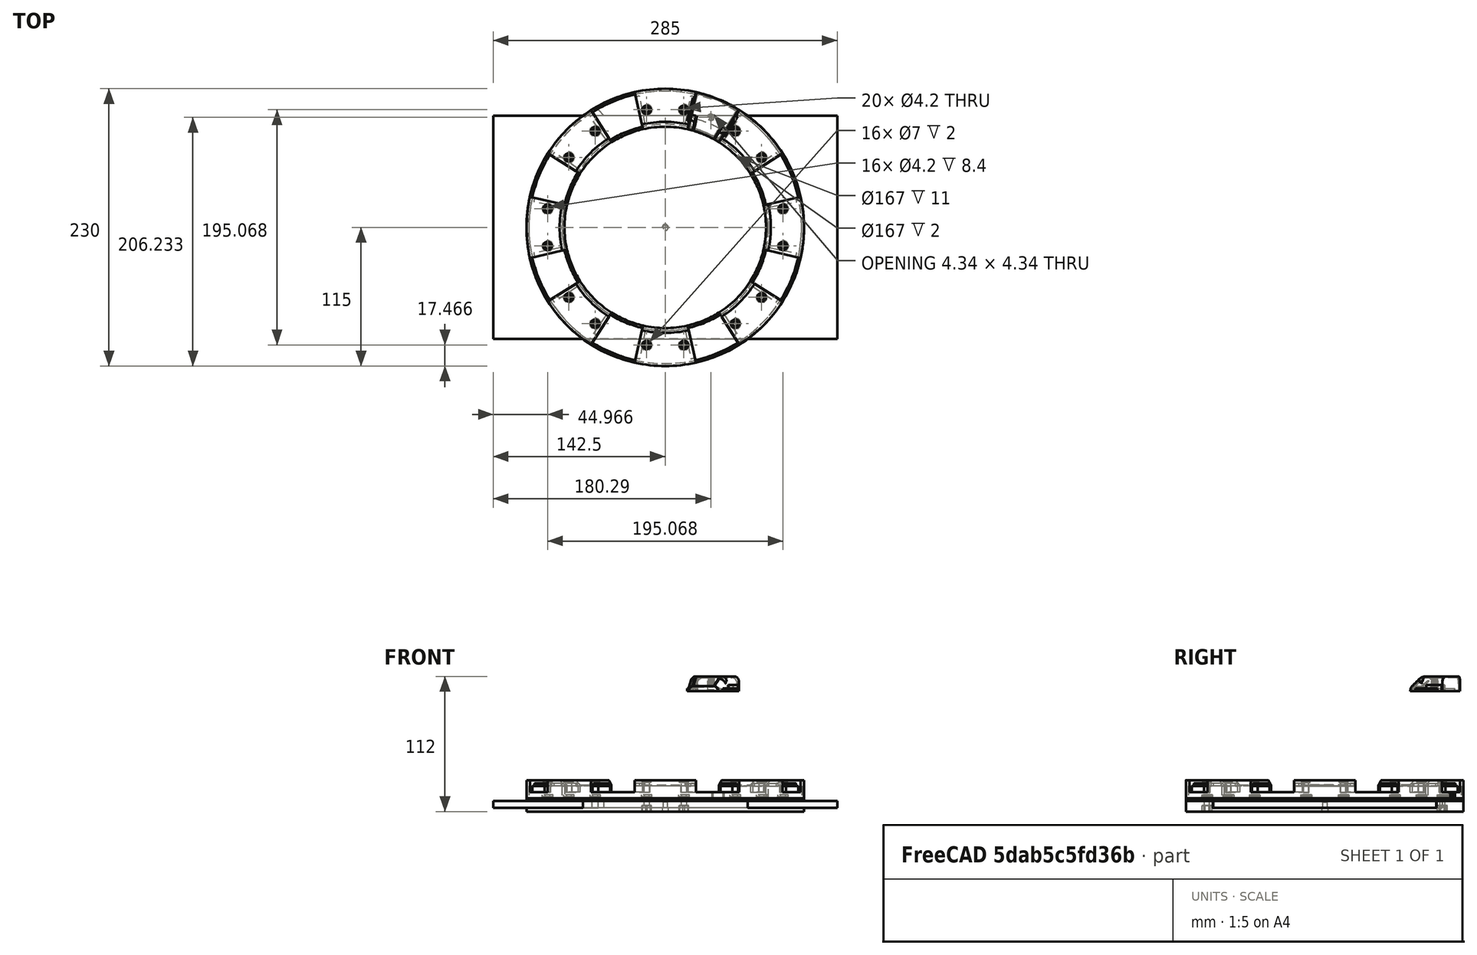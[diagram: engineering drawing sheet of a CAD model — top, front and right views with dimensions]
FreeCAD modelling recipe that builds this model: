
FCSTD DOCUMENT  (FreeCAD 1.0R39319 (Git))
Label: Mamai
License: All rights reserved
LicenseURL: https://en.wikipedia.org/wiki/All_rights_reserved
objects: Sketcher::SketchObject×45, PartDesign::Pad×23, PartDesign::Pocket×16, PartDesign::Body×8, PartDesign::Plane×7, PartDesign::Line×6, PartDesign::Fillet×6, PartDesign::Chamfer×4, PartDesign::Thickness×2, Image::ImagePlane×1, Mesh::Feature×1
note: 264 computed .brp shape members not serialized (recipe doc carries the construction recipe); baked Part::Feature solids carry a one-line shape summary decoded from their .brp

FEATURE [Image::ImagePlane] step4_tip2  label="step4-tip2"
  Placement = pos=(0,0,1000) rot=(0,0,1;0rad)
  XSize = 245
  YSize = 245
FEATURE [Mesh::Feature] pcb
  Placement = pos=(126,214.5,10) rot=(0,0,-1;1.1781rad)
FEATURE [Sketcher::SketchObject] Sketch
  ArcFitTolerance = 1e-06
  AttachmentSupport = -> [XY_Plane]
  FullyConstrained = false
  MakeInternals = false
  MapMode = 5
  sketch-geometry (10):
    g0: LineSegment StartX=0 StartY=-1e-16 StartZ=0 EndX=2e-16 EndY=-1e-16 EndZ=0
    g1: LineSegment StartX=0 StartY=-1e-16 StartZ=0 EndX=0 EndY=0 EndZ=0
    g2: LineSegment StartX=0 StartY=0 StartZ=0 EndX=2e-16 EndY=0 EndZ=0
    g3: LineSegment StartX=0 StartY=0 StartZ=0 EndX=0 EndY=-1e-16 EndZ=0
    g4: GeomPoint [constr] X=0 Y=0 Z=0
    g5: LineSegment StartX=-92.5 StartY=-142.5 StartZ=0 EndX=92.5 EndY=-142.5 EndZ=0
    g6: LineSegment StartX=92.5 StartY=-142.5 StartZ=0 EndX=92.5 EndY=142.5 EndZ=0
    g7: LineSegment StartX=92.5 StartY=142.5 StartZ=0 EndX=-92.5 EndY=142.5 EndZ=0
    g8: LineSegment StartX=-92.5 StartY=142.5 StartZ=0 EndX=-92.5 EndY=-142.5 EndZ=0
    g9: GeomPoint [constr] X=0 Y=0 Z=0
  constraints (21):
    c: Coincident(g0,g1)
    c: Coincident(g1,g2)
    c: Coincident(g2,g3)
    c: Coincident(g3,g0)
    c: Horizontal(g0)
    c: Horizontal(g2)
    c: Vertical(g1)
    c: Vertical(g3)
    c: Symmetric(g2,g0,g4)
    c: Coincident(g5,g6)
    c: Coincident(g6,g7)
    c: Coincident(g7,g8)
    c: Coincident(g8,g5)
    c: Horizontal(g5)
    c: Horizontal(g7)
    c: Vertical(g6)
    c: Vertical(g8)
    c: Symmetric(g7,g5,g9)
    c: Distance(g6,g8) = 185
    c: Distance(g5,g7) = 285
    c: Coincident(g9,g4)
FEATURE [PartDesign::Body] Body  label="Other"
  AllowCompound = false
  Group = -> [Sketch]
  Origin = -> Origin
FEATURE [Sketcher::SketchObject] Sketch001
  ArcFitTolerance = 1e-06
  AttachmentSupport = -> [XY_Plane001]
  FullyConstrained = true
  MakeInternals = false
  MapMode = 5
  sketch-geometry (5):
    g0: LineSegment StartX=-142.5 StartY=-92.5 StartZ=0 EndX=142.5 EndY=-92.5 EndZ=0
    g1: LineSegment StartX=142.5 StartY=-92.5 StartZ=0 EndX=142.5 EndY=92.5 EndZ=0
    g2: LineSegment StartX=142.5 StartY=92.5 StartZ=0 EndX=-142.5 EndY=92.5 EndZ=0
    g3: LineSegment StartX=-142.5 StartY=92.5 StartZ=0 EndX=-142.5 EndY=-92.5 EndZ=0
    g4: GeomPoint [constr] X=0 Y=0 Z=0
  constraints (12):
    c: Coincident(g0,g1)
    c: Coincident(g1,g2)
    c: Coincident(g2,g3)
    c: Coincident(g3,g0)
    c: Horizontal(g0)
    c: Horizontal(g2)
    c: Vertical(g1)
    c: Vertical(g3)
    c: Symmetric(g2,g0,g4)
    c: Distance(g1,g3) = 285
    c: Distance(g0,g2) = 185
    c: Coincident(g4,g-1)
FEATURE [PartDesign::Pad] Pad
  Direction = (0,0,1)
  Length = 5.7
  Length2 = 10
  Profile = -> Sketch001
  ReferenceAxis = -> Sketch001 [N_Axis]
  Refine = true
  Suppressed = false
  Type = 0
FEATURE [PartDesign::Body] Body001  label="Tablet"
  AllowCompound = false
  Group = -> [Sketch001,Pad]
  Origin = -> Origin001
  Placement = pos=(0,0,3) rot=(0,0,1;0rad)
  Tip = -> Pad
FEATURE [Sketcher::SketchObject] Sketch002
  ArcFitTolerance = 1e-06
  AttachmentSupport = -> [XY_Plane002]
  FullyConstrained = false
  MakeInternals = false
  MapMode = 5
  sketch-geometry (11):
    g0: LineSegment [constr] StartX=-142.5 StartY=-92.5 StartZ=0 EndX=142.5 EndY=-92.5 EndZ=0
    g1: LineSegment [constr] StartX=142.5 StartY=-92.5 StartZ=0 EndX=142.5 EndY=92.5 EndZ=0
    g2: LineSegment [constr] StartX=142.5 StartY=92.5 StartZ=0 EndX=68.3283 EndY=92.5 EndZ=0
    g3: LineSegment [constr] StartX=-142.5 StartY=92.5 StartZ=0 EndX=-142.5 EndY=-92.5 EndZ=0
    g4: GeomPoint [constr] X=0 Y=0 Z=0
    g5: LineSegment [constr] StartX=-133.5 StartY=83.5 StartZ=0 EndX=-133.5 EndY=-83.5 EndZ=0
    g6: LineSegment [constr] StartX=-133.5 StartY=-83.5 StartZ=0 EndX=133.5 EndY=-83.5 EndZ=0
    g7: LineSegment [constr] StartX=133.5 StartY=-83.5 StartZ=0 EndX=133.5 EndY=83.5 EndZ=0
    g8: LineSegment [constr] StartX=133.5 StartY=83.5 StartZ=0 EndX=-133.5 EndY=83.5 EndZ=0
    g9: LineSegment [constr] StartX=68.3283 StartY=92.5 StartZ=0 EndX=-142.5 EndY=92.5 EndZ=0
    g10: Circle CenterX=0 CenterY=0 CenterZ=0 NormalX=0 NormalY=0 NormalZ=1 AngleXU=0 Radius=115
  constraints (28):
    c: Coincident(g0,g1)
    c: Coincident(g1,g2)
    c: Coincident(g3,g0)
    c: Horizontal(g0)
    c: Horizontal(g2)
    c: Vertical(g1)
    c: Vertical(g3)
    c: Symmetric(g2,g0,g4)
    c: Distance(g1,g3) = 285
    c: Distance(g0,g3) = 185
    c: Coincident(g4,g-1)
    c: Coincident(g5,g6)
    c: Coincident(g6,g7)
    c: Coincident(g7,g8)
    c: Coincident(g8,g5)
    c: Vertical(g5)
    c: Vertical(g7)
    c: Horizontal(g6)
    c: Horizontal(g8)
    c: Distance(g3,g5) = 9
    c: Distance(g8,g2) = 9
    c: Distance(g0,g6) = 9
    c: Distance(g1,g7) = 9
    c: Coincident(g9,g2)
    c: Coincident(g9,g3)
    c: Horizontal(g9)
    c: Coincident(g10,g4)
    c: Diameter(g10) = 230
FEATURE [PartDesign::Pad] Pad001
  Direction = (0,0,1)
  Length = 8.7
  Length2 = 10
  Profile = -> Sketch002
  ReferenceAxis = -> Sketch002 [N_Axis]
  Refine = true
  Suppressed = false
  Type = 0
FEATURE [PartDesign::Plane] DatumPlane
  AttachmentOffset = pos=(115,0,0) rot=(0,1,0;1.5708rad)
  AttachmentSupport = -> [Pad001]
  Length = 71.4441
  MapMode = 45
  Placement = pos=(115,-6e-15,4.35) rot=(0,1,0;1.5708rad)
  ResizeMode = 0
  Width = 251.368
FEATURE [Sketcher::SketchObject] Sketch005
  ArcFitTolerance = 1e-06
  AttachmentSupport = -> [DatumPlane]
  FullyConstrained = true
  MakeInternals = false
  MapMode = 5
  Placement = pos=(115,-6e-15,4.35) rot=(0,1,0;1.5708rad)
  sketch-geometry (5):
    g0: LineSegment StartX=-4.35 StartY=-92.6 StartZ=0 EndX=1.35 EndY=-92.6 EndZ=0
    g1: LineSegment StartX=1.35 StartY=-92.6 StartZ=0 EndX=1.35 EndY=92.6 EndZ=0
    g2: LineSegment StartX=1.35 StartY=92.6 StartZ=0 EndX=-4.35 EndY=92.6 EndZ=0
    g3: LineSegment StartX=-4.35 StartY=92.6 StartZ=0 EndX=-4.35 EndY=-92.6 EndZ=0
    g4: GeomPoint [constr] X=-1.5 Y=0 Z=0
  constraints (13):
    c: Coincident(g0,g1)
    c: Coincident(g1,g2)
    c: Coincident(g2,g3)
    c: Coincident(g3,g0)
    c: Horizontal(g0)
    c: Horizontal(g2)
    c: Vertical(g1)
    c: Vertical(g3)
    c: Symmetric(g2,g0,g4)
    c: Distance(g1,g3) = 5.7
    c: Distance(g0,g2) = 185.2
    c: PointOnObject(g4,g-1)
    c: DistanceX(g4,g-1) = 1.5
FEATURE [PartDesign::Pocket] Pocket
  BaseFeature = -> Pad001
  Direction = (-1,0,-2e-16)
  Length = 257
  Length2 = 5
  Profile = -> Sketch005
  ReferenceAxis = -> Sketch005 [N_Axis]
  Refine = true
  Suppressed = false
  Type = 0
FEATURE [Sketcher::SketchObject] Sketch006
  ArcFitTolerance = 1e-06
  AttachmentSupport = -> [XY_Plane003]
  FullyConstrained = true
  MakeInternals = false
  MapMode = 5
  sketch-geometry (1):
    g0: Circle CenterX=0 CenterY=0 CenterZ=0 NormalX=0 NormalY=0 NormalZ=1 AngleXU=0 Radius=115
  constraints (2):
    c: Diameter(g0) = 230
    c: Coincident(g0,g-1)
FEATURE [PartDesign::Pad] Pad002
  Direction = (0,0,1)
  Length = 2
  Length2 = 10
  Profile = -> Sketch006
  ReferenceAxis = -> Sketch006 [N_Axis]
  Refine = true
  Suppressed = false
  Type = 0
FEATURE [Sketcher::SketchObject] Sketch007
  ArcFitTolerance = 1e-06
  AttachmentSupport = -> [Pad002]
  FullyConstrained = true
  MakeInternals = false
  MapMode = 5
  Placement = pos=(0,0,2) rot=(0,0,1;0rad)
  sketch-geometry (6):
    g0: Circle CenterX=0 CenterY=0 CenterZ=0 NormalX=0 NormalY=0 NormalZ=1 AngleXU=0 Radius=83.5
    g1: LineSegment [constr] StartX=-142.5 StartY=-92.5 StartZ=0 EndX=142.5 EndY=-92.5 EndZ=0
    g2: LineSegment [constr] StartX=142.5 StartY=-92.5 StartZ=0 EndX=142.5 EndY=92.5 EndZ=0
    g3: LineSegment [constr] StartX=142.5 StartY=92.5 StartZ=0 EndX=-142.5 EndY=92.5 EndZ=0
    g4: LineSegment [constr] StartX=-142.5 StartY=92.5 StartZ=0 EndX=-142.5 EndY=-92.5 EndZ=0
    g5: GeomPoint [constr] X=0 Y=0 Z=0
  constraints (14):
    c: Coincident(g0,g-1)
    c: Coincident(g1,g2)
    c: Coincident(g2,g3)
    c: Coincident(g3,g4)
    c: Coincident(g4,g1)
    c: Horizontal(g1)
    c: Horizontal(g3)
    c: Vertical(g2)
    c: Vertical(g4)
    c: Symmetric(g3,g1,g5)
    c: Distance(g2,g4) = 285
    c: Distance(g1,g3) = 185
    c: Coincident(g5,g0)
    c: Distance(g0,g3) = 9
FEATURE [PartDesign::Pocket] Pocket001
  BaseFeature = -> Pad002
  Direction = (0,0,-1)
  Length = 5
  Length2 = 5
  Profile = -> Sketch007
  ReferenceAxis = -> Sketch007 [N_Axis]
  Refine = true
  Suppressed = false
  Type = 0
FEATURE [Sketcher::SketchObject] Sketch008
  ArcFitTolerance = 1e-06
  AttachmentSupport = -> [Pocket001]
  FullyConstrained = false
  MakeInternals = false
  MapMode = 5
  Placement = pos=(0,0,2) rot=(0,0,1;0rad)
  sketch-geometry (36):
    g0: LineSegment [constr] StartX=1.9e-05 StartY=-1.44227e-05 StartZ=0 EndX=97.5342 EndY=15.4479 EndZ=0
    g1: LineSegment [constr] StartX=-1.49389e-08 StartY=-2.44401e-07 StartZ=0 EndX=79.8904 EndY=58.0438 EndZ=0
    g2: LineSegment [constr] StartX=1.9e-05 StartY=-1.44227e-05 StartZ=0 EndX=58.0438 EndY=79.8904 EndZ=0
    g3: LineSegment [constr] StartX=-1.49389e-08 StartY=-2.44401e-07 StartZ=0 EndX=15.4479 EndY=97.5342 EndZ=0
    g4: ArcOfCircle [constr] CenterX=1.9e-05 CenterY=-1.44227e-05 CenterZ=0 NormalX=0 NormalY=0 NormalZ=1 AngleXU=0 Radius=98.75 StartAngle=4.28074e-09 EndAngle=1.5708
    g5: Circle CenterX=15.4479 CenterY=97.5342 CenterZ=0 NormalX=0 NormalY=0 NormalZ=1 AngleXU=0 Radius=2.1
    g6: Circle CenterX=58.0438 CenterY=79.8904 CenterZ=0 NormalX=0 NormalY=0 NormalZ=1 AngleXU=0 Radius=2.1
    g7: Circle CenterX=79.8904 CenterY=58.0438 CenterZ=0 NormalX=0 NormalY=0 NormalZ=1 AngleXU=0 Radius=2.1
    g8: Circle CenterX=97.5342 CenterY=15.4479 CenterZ=0 NormalX=0 NormalY=0 NormalZ=1 AngleXU=0 Radius=2.1
    g9: LineSegment [constr] StartX=1.9e-05 StartY=1.44227e-05 StartZ=0 EndX=97.5342 EndY=-15.4479 EndZ=0
    g10: LineSegment [constr] StartX=-1.49389e-08 StartY=2.44401e-07 StartZ=0 EndX=79.8904 EndY=-58.0438 EndZ=0
    g11: LineSegment [constr] StartX=1.9e-05 StartY=1.44227e-05 StartZ=0 EndX=58.0438 EndY=-79.8904 EndZ=0
    g12: LineSegment [constr] StartX=-1.49389e-08 StartY=2.44401e-07 StartZ=0 EndX=15.4479 EndY=-97.5342 EndZ=0
    g13: ArcOfCircle [constr] CenterX=1.9e-05 CenterY=1.44227e-05 CenterZ=0 NormalX=0 NormalY=0 NormalZ=1 AngleXU=0 Radius=98.75 StartAngle=4.71239 EndAngle=6.28319
    g14: Circle CenterX=15.4479 CenterY=-97.5342 CenterZ=0 NormalX=0 NormalY=0 NormalZ=1 AngleXU=0 Radius=2.1
    g15: Circle CenterX=58.0438 CenterY=-79.8904 CenterZ=0 NormalX=0 NormalY=0 NormalZ=1 AngleXU=0 Radius=2.1
    g16: Circle CenterX=79.8904 CenterY=-58.0438 CenterZ=0 NormalX=0 NormalY=0 NormalZ=1 AngleXU=0 Radius=2.1
    g17: Circle CenterX=97.5342 CenterY=-15.4479 CenterZ=0 NormalX=0 NormalY=0 NormalZ=1 AngleXU=0 Radius=2.1
    g18: LineSegment [constr] StartX=-1.9e-05 StartY=-1.44227e-05 StartZ=0 EndX=-97.5342 EndY=15.4479 EndZ=0
    g19: LineSegment [constr] StartX=1.49389e-08 StartY=-2.44401e-07 StartZ=0 EndX=-79.8904 EndY=58.0438 EndZ=0
    g20: LineSegment [constr] StartX=-1.9e-05 StartY=-1.44227e-05 StartZ=0 EndX=-58.0438 EndY=79.8904 EndZ=0
    g21: LineSegment [constr] StartX=1.49389e-08 StartY=-2.44401e-07 StartZ=0 EndX=-15.4479 EndY=97.5342 EndZ=0
    g22: ArcOfCircle [constr] CenterX=-1.9e-05 CenterY=-1.44227e-05 CenterZ=0 NormalX=0 NormalY=0 NormalZ=1 AngleXU=0 Radius=98.75 StartAngle=1.5708 EndAngle=3.14159
    g23: Circle CenterX=-15.4479 CenterY=97.5342 CenterZ=0 NormalX=0 NormalY=0 NormalZ=1 AngleXU=0 Radius=2.1
    g24: Circle CenterX=-58.0438 CenterY=79.8904 CenterZ=0 NormalX=0 NormalY=0 NormalZ=1 AngleXU=0 Radius=2.1
    g25: Circle CenterX=-79.8904 CenterY=58.0438 CenterZ=0 NormalX=0 NormalY=0 NormalZ=1 AngleXU=0 Radius=2.1
    g26: Circle CenterX=-97.5342 CenterY=15.4479 CenterZ=0 NormalX=0 NormalY=0 NormalZ=1 AngleXU=0 Radius=2.1
    g27: LineSegment [constr] StartX=-1.9e-05 StartY=1.44227e-05 StartZ=0 EndX=-97.5342 EndY=-15.4479 EndZ=0
    g28: LineSegment [constr] StartX=1.49389e-08 StartY=2.44401e-07 StartZ=0 EndX=-79.8904 EndY=-58.0438 EndZ=0
    g29: LineSegment [constr] StartX=-1.9e-05 StartY=1.44227e-05 StartZ=0 EndX=-58.0438 EndY=-79.8904 EndZ=0
    g30: LineSegment [constr] StartX=1.49389e-08 StartY=2.44401e-07 StartZ=0 EndX=-15.4479 EndY=-97.5342 EndZ=0
    g31: ArcOfCircle [constr] CenterX=-1.9e-05 CenterY=1.44227e-05 CenterZ=0 NormalX=0 NormalY=0 NormalZ=1 AngleXU=0 Radius=98.75 StartAngle=3.14159 EndAngle=4.71239
    g32: Circle CenterX=-15.4479 CenterY=-97.5342 CenterZ=0 NormalX=0 NormalY=0 NormalZ=1 AngleXU=0 Radius=2.1
    g33: Circle CenterX=-58.0438 CenterY=-79.8904 CenterZ=0 NormalX=0 NormalY=0 NormalZ=1 AngleXU=0 Radius=2.1
    g34: Circle CenterX=-79.8904 CenterY=-58.0438 CenterZ=0 NormalX=0 NormalY=0 NormalZ=1 AngleXU=0 Radius=2.1
    g35: Circle CenterX=-97.5342 CenterY=-15.4479 CenterZ=0 NormalX=0 NormalY=0 NormalZ=1 AngleXU=0 Radius=2.1
  constraints (49):
    c: Angle(g-1,g0) = 0.15708
    c: Angle(g-1,g1) = 0.628319
    c: Angle(g-1,g2) = 0.942478
    c: Angle(g-1,g3) = 1.41372
    c: Radius(g4) = 98.75
    c: PointOnObject(g4,g-2)
    c: PointOnObject(g3,g4)
    c: PointOnObject(g2,g4)
    c: PointOnObject(g1,g4)
    c: PointOnObject(g0,g4)
    c: Diameter(g5) = 4.2
    c: Coincident(g5,g3)
    c: Diameter(g6) = 4.2
    c: Diameter(g7) = 4.2
    c: Diameter(g8) = 4.2
    c: Coincident(g8,g0)
    c: Radius(g13) = 98.75
    c: PointOnObject(g12,g13)
    c: PointOnObject(g11,g13)
    c: PointOnObject(g10,g13)
    c: PointOnObject(g9,g13)
    c: Diameter(g14) = 4.2
    c: Coincident(g14,g12)
    c: Diameter(g15) = 4.2
    c: Diameter(g16) = 4.2
    c: Diameter(g17) = 4.2
    c: Coincident(g17,g9)
    c: Radius(g22) = 98.75
    c: PointOnObject(g21,g22)
    c: PointOnObject(g20,g22)
    c: PointOnObject(g19,g22)
    c: PointOnObject(g18,g22)
    c: Diameter(g23) = 4.2
    c: Coincident(g23,g21)
    c: Diameter(g24) = 4.2
    c: Diameter(g25) = 4.2
    c: Diameter(g26) = 4.2
    c: Coincident(g26,g18)
    c: Radius(g31) = 98.75
    c: PointOnObject(g30,g31)
    c: PointOnObject(g29,g31)
    c: PointOnObject(g28,g31)
    c: PointOnObject(g27,g31)
    c: Diameter(g32) = 4.2
    c: Coincident(g32,g30)
    c: Diameter(g33) = 4.2
    c: Diameter(g34) = 4.2
    c: Diameter(g35) = 4.2
    c: Coincident(g35,g27)
FEATURE [PartDesign::Pocket] Pocket002
  BaseFeature = -> Pocket001
  Direction = (0,0,-1)
  Length = 5
  Length2 = 5
  Profile = -> Sketch008
  ReferenceAxis = -> Sketch008 [N_Axis]
  Refine = true
  Suppressed = false
  Type = 0
FEATURE [Sketcher::SketchObject] Sketch009
  ArcFitTolerance = 1e-06
  AttachmentSupport = -> [Pocket002]
  FullyConstrained = false
  MakeInternals = false
  MapMode = 5
  Placement = pos=(0,0,2) rot=(0,0,1;0rad)
  sketch-geometry (52):
    g0: LineSegment [constr] StartX=0 StartY=0 StartZ=0 EndX=97.5342 EndY=15.4479 EndZ=0
    g1: LineSegment [constr] StartX=0 StartY=0 StartZ=0 EndX=58.0438 EndY=79.8904 EndZ=0
    g2: LineSegment [constr] StartX=-8.8e-15 StartY=-1.05361e-11 StartZ=0 EndX=15.4479 EndY=97.5342 EndZ=0
    g3: ArcOfCircle [constr] CenterX=-8.8e-15 CenterY=-1.05361e-11 CenterZ=0 NormalX=0 NormalY=0 NormalZ=1 AngleXU=0 Radius=98.75 StartAngle=1.067e-13 EndAngle=1.5708
    g4: Circle CenterX=15.4479 CenterY=97.5342 CenterZ=0 NormalX=0 NormalY=0 NormalZ=1 AngleXU=0 Radius=4.5
    g5: Circle CenterX=15.4479 CenterY=97.5342 CenterZ=0 NormalX=0 NormalY=0 NormalZ=1 AngleXU=0 Radius=2.1
    g6: Circle CenterX=58.0438 CenterY=79.8904 CenterZ=0 NormalX=0 NormalY=0 NormalZ=1 AngleXU=0 Radius=2.1
    g7: Circle CenterX=58.0438 CenterY=79.8904 CenterZ=0 NormalX=0 NormalY=0 NormalZ=1 AngleXU=0 Radius=4.5
    g8: LineSegment [constr] StartX=0 StartY=0 StartZ=0 EndX=79.8904 EndY=58.0438 EndZ=0
    g9: Circle CenterX=79.8904 CenterY=58.0438 CenterZ=0 NormalX=0 NormalY=0 NormalZ=1 AngleXU=0 Radius=2.1
    g10: Circle CenterX=79.8904 CenterY=58.0438 CenterZ=0 NormalX=0 NormalY=0 NormalZ=1 AngleXU=0 Radius=4.5
    g11: Circle CenterX=97.5342 CenterY=15.4479 CenterZ=0 NormalX=0 NormalY=0 NormalZ=1 AngleXU=0 Radius=2.1
    g12: Circle CenterX=97.5342 CenterY=15.4479 CenterZ=0 NormalX=0 NormalY=0 NormalZ=1 AngleXU=0 Radius=4.5
    g13: LineSegment [constr] StartX=0 StartY=0 StartZ=0 EndX=97.5342 EndY=-15.4479 EndZ=0
    g14: LineSegment [constr] StartX=0 StartY=0 StartZ=0 EndX=58.0438 EndY=-79.8904 EndZ=0
    g15: LineSegment [constr] StartX=-8.8e-15 StartY=1.05361e-11 StartZ=0 EndX=15.4479 EndY=-97.5342 EndZ=0
    g16: ArcOfCircle [constr] CenterX=-8.8e-15 CenterY=1.05361e-11 CenterZ=0 NormalX=0 NormalY=0 NormalZ=1 AngleXU=0 Radius=98.75 StartAngle=4.71239 EndAngle=6.28319
    g17: Circle CenterX=15.4479 CenterY=-97.5342 CenterZ=0 NormalX=0 NormalY=0 NormalZ=1 AngleXU=0 Radius=4.5
    g18: Circle CenterX=15.4479 CenterY=-97.5342 CenterZ=0 NormalX=0 NormalY=0 NormalZ=1 AngleXU=0 Radius=2.1
    g19: Circle CenterX=58.0438 CenterY=-79.8904 CenterZ=0 NormalX=0 NormalY=0 NormalZ=1 AngleXU=0 Radius=2.1
    g20: Circle CenterX=58.0438 CenterY=-79.8904 CenterZ=0 NormalX=0 NormalY=0 NormalZ=1 AngleXU=0 Radius=4.5
    g21: LineSegment [constr] StartX=0 StartY=0 StartZ=0 EndX=79.8904 EndY=-58.0438 EndZ=0
    g22: Circle CenterX=79.8904 CenterY=-58.0438 CenterZ=0 NormalX=0 NormalY=0 NormalZ=1 AngleXU=0 Radius=2.1
    g23: Circle CenterX=79.8904 CenterY=-58.0438 CenterZ=0 NormalX=0 NormalY=0 NormalZ=1 AngleXU=0 Radius=4.5
    g24: Circle CenterX=97.5342 CenterY=-15.4479 CenterZ=0 NormalX=0 NormalY=0 NormalZ=1 AngleXU=0 Radius=2.1
    g25: Circle CenterX=97.5342 CenterY=-15.4479 CenterZ=0 NormalX=0 NormalY=0 NormalZ=1 AngleXU=0 Radius=4.5
    g26: LineSegment [constr] StartX=0 StartY=0 StartZ=0 EndX=-97.5342 EndY=15.4479 EndZ=0
    g27: LineSegment [constr] StartX=0 StartY=0 StartZ=0 EndX=-58.0438 EndY=79.8904 EndZ=0
    g28: LineSegment [constr] StartX=8.8e-15 StartY=-1.05361e-11 StartZ=0 EndX=-15.4479 EndY=97.5342 EndZ=0
    g29: ArcOfCircle [constr] CenterX=8.8e-15 CenterY=-1.05361e-11 CenterZ=0 NormalX=0 NormalY=0 NormalZ=1 AngleXU=0 Radius=98.75 StartAngle=1.5708 EndAngle=3.14159
    g30: Circle CenterX=-15.4479 CenterY=97.5342 CenterZ=0 NormalX=0 NormalY=0 NormalZ=1 AngleXU=0 Radius=4.5
    g31: Circle CenterX=-15.4479 CenterY=97.5342 CenterZ=0 NormalX=0 NormalY=0 NormalZ=1 AngleXU=0 Radius=2.1
    g32: Circle CenterX=-58.0438 CenterY=79.8904 CenterZ=0 NormalX=0 NormalY=0 NormalZ=1 AngleXU=0 Radius=2.1
    g33: Circle CenterX=-58.0438 CenterY=79.8904 CenterZ=0 NormalX=0 NormalY=0 NormalZ=1 AngleXU=0 Radius=4.5
    g34: LineSegment [constr] StartX=0 StartY=0 StartZ=0 EndX=-79.8904 EndY=58.0438 EndZ=0
    g35: Circle CenterX=-79.8904 CenterY=58.0438 CenterZ=0 NormalX=0 NormalY=0 NormalZ=1 AngleXU=0 Radius=2.1
    g36: Circle CenterX=-79.8904 CenterY=58.0438 CenterZ=0 NormalX=0 NormalY=0 NormalZ=1 AngleXU=0 Radius=4.5
    g37: Circle CenterX=-97.5342 CenterY=15.4479 CenterZ=0 NormalX=0 NormalY=0 NormalZ=1 AngleXU=0 Radius=2.1
    g38: Circle CenterX=-97.5342 CenterY=15.4479 CenterZ=0 NormalX=0 NormalY=0 NormalZ=1 AngleXU=0 Radius=4.5
    g39: LineSegment [constr] StartX=0 StartY=0 StartZ=0 EndX=-97.5342 EndY=-15.4479 EndZ=0
    g40: LineSegment [constr] StartX=0 StartY=0 StartZ=0 EndX=-58.0438 EndY=-79.8904 EndZ=0
    g41: LineSegment [constr] StartX=8.8e-15 StartY=1.05361e-11 StartZ=0 EndX=-15.4479 EndY=-97.5342 EndZ=0
    g42: ArcOfCircle [constr] CenterX=8.8e-15 CenterY=1.05361e-11 CenterZ=0 NormalX=0 NormalY=0 NormalZ=1 AngleXU=0 Radius=98.75 StartAngle=3.14159 EndAngle=4.71239
    g43: Circle CenterX=-15.4479 CenterY=-97.5342 CenterZ=0 NormalX=0 NormalY=0 NormalZ=1 AngleXU=0 Radius=4.5
    g44: Circle CenterX=-15.4479 CenterY=-97.5342 CenterZ=0 NormalX=0 NormalY=0 NormalZ=1 AngleXU=0 Radius=2.1
    g45: Circle CenterX=-58.0438 CenterY=-79.8904 CenterZ=0 NormalX=0 NormalY=0 NormalZ=1 AngleXU=0 Radius=2.1
    g46: Circle CenterX=-58.0438 CenterY=-79.8904 CenterZ=0 NormalX=0 NormalY=0 NormalZ=1 AngleXU=0 Radius=4.5
    g47: LineSegment [constr] StartX=0 StartY=0 StartZ=0 EndX=-79.8904 EndY=-58.0438 EndZ=0
    g48: Circle CenterX=-79.8904 CenterY=-58.0438 CenterZ=0 NormalX=0 NormalY=0 NormalZ=1 AngleXU=0 Radius=2.1
    g49: Circle CenterX=-79.8904 CenterY=-58.0438 CenterZ=0 NormalX=0 NormalY=0 NormalZ=1 AngleXU=0 Radius=4.5
    g50: Circle CenterX=-97.5342 CenterY=-15.4479 CenterZ=0 NormalX=0 NormalY=0 NormalZ=1 AngleXU=0 Radius=2.1
    g51: Circle CenterX=-97.5342 CenterY=-15.4479 CenterZ=0 NormalX=0 NormalY=0 NormalZ=1 AngleXU=0 Radius=4.5
  constraints (77):
    c: Angle(g-1,g0) = 0.15708
    c: Angle(g-1,g1) = 0.942478
    c: Angle(g-1,g2) = 1.41372
    c: Radius(g3) = 98.75
    c: PointOnObject(g3,g-2)
    c: PointOnObject(g2,g3)
    c: PointOnObject(g1,g3)
    c: PointOnObject(g0,g3)
    c: Diameter(g4) = 9
    c: Coincident(g4,g2)
    c: Diameter(g5) = 4.2
    c: Coincident(g5,g2)
    c: Diameter(g6) = 4.2
    c: Coincident(g6,g1)
    c: Diameter(g7) = 9
    c: Angle(g-1,g8) = 0.628319
    c: PointOnObject(g8,g3)
    c: Diameter(g9) = 4.2
    c: Coincident(g9,g8)
    c: Diameter(g10) = 9
    c: Diameter(g11) = 4.2
    c: Coincident(g11,g0)
    c: Diameter(g12) = 9
    c: Radius(g16) = 98.75
    c: PointOnObject(g15,g16)
    c: PointOnObject(g14,g16)
    c: PointOnObject(g13,g16)
    c: Diameter(g17) = 9
    c: Coincident(g17,g15)
    c: Diameter(g18) = 4.2
    c: Coincident(g18,g15)
    c: Diameter(g19) = 4.2
    c: Coincident(g19,g14)
    c: Diameter(g20) = 9
    c: PointOnObject(g21,g16)
    c: Diameter(g22) = 4.2
    c: Coincident(g22,g21)
    c: Diameter(g23) = 9
    c: Diameter(g24) = 4.2
    c: Coincident(g24,g13)
    c: Diameter(g25) = 9
    c: Radius(g29) = 98.75
    c: PointOnObject(g28,g29)
    c: PointOnObject(g27,g29)
    c: PointOnObject(g26,g29)
    c: Diameter(g30) = 9
    c: Coincident(g30,g28)
    c: Diameter(g31) = 4.2
    c: Coincident(g31,g28)
    c: Diameter(g32) = 4.2
    c: Coincident(g32,g27)
    c: Diameter(g33) = 9
    c: PointOnObject(g34,g29)
    c: Diameter(g35) = 4.2
    c: Coincident(g35,g34)
    c: Diameter(g36) = 9
    c: Diameter(g37) = 4.2
    c: Coincident(g37,g26)
    c: Diameter(g38) = 9
    c: Radius(g42) = 98.75
    c: PointOnObject(g41,g42)
    c: PointOnObject(g40,g42)
    c: PointOnObject(g39,g42)
    c: Diameter(g43) = 9
    c: Coincident(g43,g41)
    c: Diameter(g44) = 4.2
    c: Coincident(g44,g41)
    c: Diameter(g45) = 4.2
    c: Coincident(g45,g40)
    c: Diameter(g46) = 9
    c: PointOnObject(g47,g42)
    c: Diameter(g48) = 4.2
    c: Coincident(g48,g47)
    c: Diameter(g49) = 9
    c: Diameter(g50) = 4.2
    c: Coincident(g50,g39)
    c: Diameter(g51) = 9
FEATURE [Sketcher::SketchObject] Sketch010
  ArcFitTolerance = 1e-06
  AttachmentSupport = -> [XY_Plane004]
  FullyConstrained = true
  MakeInternals = false
  MapMode = 5
  sketch-geometry (1):
    g0: Circle CenterX=0 CenterY=0 CenterZ=0 NormalX=0 NormalY=0 NormalZ=1 AngleXU=0 Radius=2.5
  constraints (2):
    c: Diameter(g0) = 5
    c: Coincident(g0,g-1)
FEATURE [PartDesign::Pad] Pad004
  Direction = (0,0,1)
  Length = 3
  Length2 = 10
  Profile = -> Sketch010
  ReferenceAxis = -> Sketch010 [N_Axis]
  Refine = true
  Suppressed = false
  Type = 0
FEATURE [Sketcher::SketchObject] Sketch011
  ArcFitTolerance = 1e-06
  AttachmentSupport = -> [Pad004]
  FullyConstrained = true
  MakeInternals = false
  MapMode = 5
  Placement = pos=(0,0,3) rot=(0,0,1;0rad)
  sketch-geometry (1):
    g0: Circle CenterX=0 CenterY=0 CenterZ=0 NormalX=0 NormalY=0 NormalZ=1 AngleXU=0 Radius=1.85
  constraints (2):
    c: Diameter(g0) = 3.7
    c: Coincident(g0,g-1)
FEATURE [PartDesign::Pad] Pad005
  BaseFeature = -> Pad004
  Direction = (0,0,1)
  Length = 4.7
  Length2 = 10
  Profile = -> Sketch011
  ReferenceAxis = -> Sketch011 [N_Axis]
  Refine = true
  Suppressed = false
  Type = 0
FEATURE [PartDesign::Body] Body004  label="TestingLockingPin"
  AllowCompound = false
  Group = -> [Sketch010,Pad004,Sketch011,Pad005]
  Origin = -> Origin004
  Tip = -> Pad005
FEATURE [Sketcher::SketchObject] Sketch014
  ArcFitTolerance = 1e-06
  AttachmentSupport = -> [XY_Plane005]
  FullyConstrained = false
  MakeInternals = false
  MapMode = 5
  sketch-geometry (5):
    g0: LineSegment [constr] StartX=0 StartY=0 StartZ=0 EndX=37.5987 EndY=90.7712 EndZ=0
    g1: ArcOfCircle CenterX=0 CenterY=0 CenterZ=0 NormalX=0 NormalY=0 NormalZ=1 AngleXU=0 Radius=83.5 StartAngle=1.01229 EndAngle=1.3439
    g2: ArcOfCircle CenterX=0 CenterY=0 CenterZ=0 NormalX=0 NormalY=0 NormalZ=1 AngleXU=0 Radius=115 StartAngle=1.01229 EndAngle=1.3439
    g3: LineSegment StartX=44.2483 StartY=70.812 StartZ=0 EndX=60.9407 EndY=97.5255 EndZ=0
    g4: LineSegment StartX=18.7834 StartY=81.3599 StartZ=0 EndX=25.8694 EndY=112.053 EndZ=0
  constraints (13):
    c: Distance(g0) = 98.25
    c: Angle(g-1,g0) = 1.1781
    c: Coincident(g0,g-1)
    c: Diameter(g1) = 167
    c: Coincident(g1,g0)
    c: Diameter(g2) = 230
    c: Coincident(g2,g0)
    c: Angle(g3,g0) = 0.165806
    c: Angle(g0,g4) = 0.165806
    c: Coincident(g4,g2)
    c: Coincident(g3,g2)
    c: Coincident(g3,g1)
    c: Coincident(g4,g1)
FEATURE [PartDesign::Pad] Pad006
  Direction = (0,0,1)
  Length = 12
  Length2 = 10
  Profile = -> Sketch014
  ReferenceAxis = -> Sketch014 [N_Axis]
  Refine = true
  Suppressed = false
  Type = 0
FEATURE [PartDesign::Chamfer] Chamfer
  Angle = 50
  Base = -> Pad006 [Edge7]
  BaseFeature = -> Pad006
  ChamferType = 2
  FlipDirection = false
  Refine = true
  Size = 8
  Size2 = 1
  SupportTransform = false
  Suppressed = false
  UseAllEdges = false
FEATURE [PartDesign::Thickness] Thickness
  Base = -> Chamfer [Face4]
  BaseFeature = -> Chamfer
  Intersection = false
  Join = 0
  Mode = 0
  Refine = true
  Reversed = true
  SupportTransform = false
  Suppressed = false
  Value = 1
FEATURE [Sketcher::SketchObject] Sketch015
  ArcFitTolerance = 1e-06
  AttachmentSupport = -> [Thickness]
  FullyConstrained = false
  MakeInternals = false
  MapMode = 5
  Placement = pos=(0,0,11) rot=(1,0,0;3.14159rad)
  sketch-geometry (17):
    g0: LineSegment [constr] StartX=0 StartY=0 StartZ=0 EndX=37.79 EndY=-91.2331 EndZ=0
    g1: Circle CenterX=37.79 CenterY=-91.2331 CenterZ=0 NormalX=0 NormalY=0 NormalZ=1 AngleXU=0 Radius=2.6
    g2: LineSegment StartX=39.5123 StartY=-89.8901 StartZ=0 EndX=38.1215 EndY=-90.452 EndZ=0
    g3: LineSegment StartX=37.5596 StartY=-89.0613 StartZ=0 EndX=36.447 EndY=-89.5108 EndZ=0
    g4: GeomPoint [constr] X=37.79 Y=-91.2331 Z=0
    g5: GeomPoint [constr] X=37.79 Y=-91.2331 Z=0
    g6: LineSegment StartX=36.0677 StartY=-92.5761 StartZ=0 EndX=37.4584 EndY=-92.0142 EndZ=0
    g7: LineSegment StartX=39.9618 StartY=-91.0027 StartZ=0 EndX=39.5123 EndY=-89.8901 EndZ=0
    g8: LineSegment StartX=35.6181 StartY=-91.4635 StartZ=0 EndX=36.0677 EndY=-92.5761 EndZ=0
    g9: GeomPoint [constr] X=37.79 Y=-91.2331 Z=0
    g10: LineSegment StartX=38.0204 StartY=-93.405 StartZ=0 EndX=39.133 EndY=-92.9554 EndZ=0
    g11: LineSegment StartX=39.133 StartY=-92.9554 StartZ=0 EndX=38.5711 EndY=-91.5647 EndZ=0
    g12: LineSegment StartX=36.447 StartY=-89.5108 StartZ=0 EndX=37.0089 EndY=-90.9016 EndZ=0
    g13: LineSegment StartX=37.0089 StartY=-90.9016 StartZ=0 EndX=35.6181 EndY=-91.4635 EndZ=0
    g14: LineSegment StartX=37.4584 StartY=-92.0142 StartZ=0 EndX=38.0204 EndY=-93.405 EndZ=0
    g15: LineSegment StartX=38.1215 StartY=-90.452 StartZ=0 EndX=37.5596 EndY=-89.0613 EndZ=0
    g16: LineSegment StartX=38.5711 StartY=-91.5647 StartZ=0 EndX=39.9618 EndY=-91.0027 EndZ=0
  constraints (25):
    c: Distance(g0) = 98.75
    c: Angle(g-1,g0) = -1.1781
    c: Coincident(g0,g-1)
    c: Diameter(g1) = 5.2
    c: Coincident(g16,g7)
    c: Coincident(g7,g2)
    c: Coincident(g13,g8)
    c: Coincident(g8,g6)
    c: Symmetric(g2,g6,g9)
    c: Distance(g7,g8) = 4.2
    c: Distance(g6,g13) = 1.2
    c: Coincident(g9,g1)
    c: Coincident(g10,g11)
    c: Coincident(g15,g3)
    c: Coincident(g3,g12)
    c: Coincident(g14,g10)
    c: Symmetric(g3,g10,g4)
    c: Distance(g11,g14) = 1.2
    c: Distance(g10,g3) = 4.2
    c: PointOnObject(g2,g15)
    c: Coincident(g12,g13)
    c: PointOnObject(g11,g16)
    c: PointOnObject(g15,g2)
    c: Coincident(g6,g14)
    c: PointOnObject(g16,g11)
FEATURE [PartDesign::Pad] Pad007
  BaseFeature = -> Thickness
  Direction = (0,0,-1)
  Length = 10
  Length2 = 10
  Profile = -> Sketch015
  ReferenceAxis = -> Sketch015 [N_Axis]
  Refine = true
  Suppressed = false
  Type = 0
FEATURE [PartDesign::Pad] Pad008
  BaseFeature = -> Pocket002
  Direction = (0,0,1)
  Length = 3
  Length2 = 10
  Profile = -> Sketch009
  ReferenceAxis = -> Sketch009 [N_Axis]
  Refine = true
  Suppressed = false
  Type = 0
FEATURE [Sketcher::SketchObject] Sketch016
  ArcFitTolerance = 1e-06
  AttachmentSupport = -> [Pocket]
  FullyConstrained = false
  MakeInternals = false
  MapMode = 5
  Placement = pos=(0,92.6,0) rot=(1,0,0;1.5708rad)
  sketch-geometry (4):
    g0: LineSegment StartX=-68.398 StartY=9 StartZ=0 EndX=-68.398 EndY=3 EndZ=0
    g1: LineSegment StartX=-68.398 StartY=3 StartZ=0 EndX=-55.398 EndY=3 EndZ=0
    g2: LineSegment StartX=-55.398 StartY=3 StartZ=0 EndX=-55.398 EndY=9 EndZ=0
    g3: LineSegment StartX=-55.398 StartY=9 StartZ=0 EndX=-68.398 EndY=9 EndZ=0
  constraints (11):
    c: Coincident(g0,g1)
    c: Coincident(g1,g2)
    c: Coincident(g2,g3)
    c: Coincident(g3,g0)
    c: Vertical(g0)
    c: Vertical(g2)
    c: Horizontal(g1)
    c: Horizontal(g3)
    c: Distance(g-1,g1) = 3
    c: DistanceY(g0,g0) = 6
    c: Distance(g3,g3) = 13
FEATURE [PartDesign::Pocket] Pocket004
  BaseFeature = -> Pocket
  Direction = (0,1,-2e-16)
  Length = 5
  Length2 = 5
  Profile = -> Sketch016
  ReferenceAxis = -> Sketch016 [N_Axis]
  Refine = true
  Suppressed = false
  Type = 0
FEATURE [PartDesign::Chamfer] Chamfer001
  Angle = 47
  Base = -> Pocket004 [Edge20]
  BaseFeature = -> Pocket004
  ChamferType = 2
  FlipDirection = false
  Refine = true
  Size = 4.6
  Size2 = 1
  SupportTransform = false
  Suppressed = false
  UseAllEdges = false
FEATURE [Sketcher::SketchObject] Sketch017
  ArcFitTolerance = 1e-06
  AttachmentSupport = -> [Chamfer001]
  FullyConstrained = true
  MakeInternals = false
  MapMode = 5
  Placement = pos=(0,0,8.7) rot=(0,0,1;0rad)
FEATURE [Sketcher::SketchObject] Sketch018
  ArcFitTolerance = 1e-06
  AttachmentSupport = -> [Chamfer001]
  FullyConstrained = false
  MakeInternals = false
  MapMode = 5
  Placement = pos=(0,0,8.7) rot=(0,0,1;0rad)
  sketch-geometry (4):
    g0: LineSegment [constr] StartX=0 StartY=0 StartZ=0 EndX=15.4479 EndY=97.5342 EndZ=0
    g1: Circle CenterX=15.4479 CenterY=97.5342 CenterZ=0 NormalX=0 NormalY=0 NormalZ=1 AngleXU=0 Radius=2.1
    g2: LineSegment [constr] StartX=0 StartY=2.99277e-07 StartZ=0 EndX=-15.4479 EndY=97.5342 EndZ=0
    g3: Circle CenterX=-15.4479 CenterY=97.5342 CenterZ=0 NormalX=0 NormalY=0 NormalZ=1 AngleXU=0 Radius=2.1
  constraints (8):
    c: Distance(g0) = 98.75
    c: Angle(g-1,g0) = 1.41372
    c: Coincident(g0,g-1)
    c: Diameter(g1) = 4.2
    c: Coincident(g1,g0)
    c: Distance(g2) = 98.75
    c: Diameter(g3) = 4.2
    c: Coincident(g3,g2)
FEATURE [PartDesign::Pocket] Pocket005
  BaseFeature = -> Chamfer001
  Direction = (0,0,-1)
  Length = 10
  Length2 = 5
  Profile = -> Sketch018
  ReferenceAxis = -> Sketch018 [N_Axis]
  Refine = true
  Suppressed = false
  Type = 0
FEATURE [Sketcher::SketchObject] Sketch019
  ArcFitTolerance = 1e-06
  AttachmentSupport = -> [Pocket005]
  FullyConstrained = false
  MakeInternals = false
  MapMode = 5
  Placement = pos=(0,0,8.7) rot=(0,0,1;0rad)
  sketch-geometry (4):
    g0: LineSegment [constr] StartX=0 StartY=0 StartZ=0 EndX=-15.4479 EndY=-97.5342 EndZ=0
    g1: Circle CenterX=-15.4479 CenterY=-97.5342 CenterZ=0 NormalX=0 NormalY=0 NormalZ=1 AngleXU=0 Radius=2.1
    g2: Circle CenterX=15.4479 CenterY=-97.5342 CenterZ=0 NormalX=0 NormalY=0 NormalZ=1 AngleXU=0 Radius=2.1
    g3: LineSegment [constr] StartX=0 StartY=5.94506e-08 StartZ=0 EndX=15.4479 EndY=-97.5342 EndZ=0
  constraints (8):
    c: Distance(g0) = 98.75
    c: Angle(g-1,g0) = -1.72788
    c: Coincident(g0,g-1)
    c: Diameter(g1) = 4.2
    c: Coincident(g1,g0)
    c: Distance(g3) = 98.75
    c: Diameter(g2) = 4.2
    c: Coincident(g2,g3)
FEATURE [PartDesign::Pocket] Pocket006
  BaseFeature = -> Pocket005
  Direction = (0,0,-1)
  Length = 10
  Length2 = 5
  Profile = -> Sketch019
  ReferenceAxis = -> Sketch019 [N_Axis]
  Refine = true
  Suppressed = false
  Type = 0
FEATURE [Sketcher::SketchObject] Sketch020
  ArcFitTolerance = 1e-06
  AttachmentSupport = -> [Pocket006]
  FullyConstrained = false
  MakeInternals = false
  MapMode = 5
  Placement = pos=(0,0,0) rot=(1,0,0;3.14159rad)
  sketch-geometry (32):
    g0: LineSegment [constr] StartX=0 StartY=0 StartZ=0 EndX=15.4479 EndY=97.5342 EndZ=0
    g1: LineSegment StartX=14.7909 StartY=93.3859 StartZ=0 EndX=18.7119 EndY=94.8911 EndZ=0
    g2: LineSegment StartX=18.7119 StartY=94.8911 StartZ=0 EndX=19.3689 EndY=99.0394 EndZ=0
    g3: LineSegment StartX=19.3689 StartY=99.0394 StartZ=0 EndX=16.1049 EndY=101.683 EndZ=0
    g4: LineSegment StartX=16.1049 StartY=101.683 StartZ=0 EndX=12.1839 EndY=100.177 EndZ=0
    g5: LineSegment StartX=12.1839 StartY=100.177 StartZ=0 EndX=11.5268 EndY=96.0291 EndZ=0
    g6: LineSegment StartX=11.5268 StartY=96.0291 StartZ=0 EndX=14.7909 EndY=93.3859 EndZ=0
    g7: Circle [constr] CenterX=15.4479 CenterY=97.5342 CenterZ=0 NormalX=0 NormalY=0 NormalZ=1 AngleXU=0 Radius=4.2
    g8: LineSegment [constr] StartX=0 StartY=-7.30715e-09 StartZ=0 EndX=15.4479 EndY=-97.5342 EndZ=0
    g9: LineSegment StartX=14.7909 StartY=-93.3859 StartZ=0 EndX=18.7119 EndY=-94.8911 EndZ=0
    g10: LineSegment StartX=18.7119 StartY=-94.8911 StartZ=0 EndX=19.3689 EndY=-99.0394 EndZ=0
    g11: LineSegment StartX=19.3689 StartY=-99.0394 StartZ=0 EndX=16.1049 EndY=-101.683 EndZ=0
    g12: LineSegment StartX=16.1049 StartY=-101.683 StartZ=0 EndX=12.1839 EndY=-100.177 EndZ=0
    g13: LineSegment StartX=12.1839 StartY=-100.177 StartZ=0 EndX=11.5268 EndY=-96.0291 EndZ=0
    g14: LineSegment StartX=11.5268 StartY=-96.0291 StartZ=0 EndX=14.7909 EndY=-93.3859 EndZ=0
    g15: Circle [constr] CenterX=15.4479 CenterY=-97.5342 CenterZ=0 NormalX=0 NormalY=0 NormalZ=1 AngleXU=0 Radius=4.2
    g16: LineSegment [constr] StartX=0 StartY=0 StartZ=0 EndX=-15.4479 EndY=97.5342 EndZ=0
    g17: LineSegment StartX=-14.7909 StartY=93.3859 StartZ=0 EndX=-18.7119 EndY=94.8911 EndZ=0
    g18: LineSegment StartX=-18.7119 StartY=94.8911 StartZ=0 EndX=-19.3689 EndY=99.0394 EndZ=0
    g19: LineSegment StartX=-19.3689 StartY=99.0394 StartZ=0 EndX=-16.1049 EndY=101.683 EndZ=0
    g20: LineSegment StartX=-16.1049 StartY=101.683 StartZ=0 EndX=-12.1839 EndY=100.177 EndZ=0
    g21: LineSegment StartX=-12.1839 StartY=100.177 StartZ=0 EndX=-11.5268 EndY=96.0291 EndZ=0
    g22: LineSegment StartX=-11.5268 StartY=96.0291 StartZ=0 EndX=-14.7909 EndY=93.3859 EndZ=0
    g23: Circle [constr] CenterX=-15.4479 CenterY=97.5342 CenterZ=0 NormalX=0 NormalY=0 NormalZ=1 AngleXU=0 Radius=4.2
    g24: LineSegment [constr] StartX=0 StartY=-7.30715e-09 StartZ=0 EndX=-15.4479 EndY=-97.5342 EndZ=0
    g25: LineSegment StartX=-14.7909 StartY=-93.3859 StartZ=0 EndX=-18.7119 EndY=-94.8911 EndZ=0
    g26: LineSegment StartX=-18.7119 StartY=-94.8911 StartZ=0 EndX=-19.3689 EndY=-99.0394 EndZ=0
    g27: LineSegment StartX=-19.3689 StartY=-99.0394 StartZ=0 EndX=-16.1049 EndY=-101.683 EndZ=0
    g28: LineSegment StartX=-16.1049 StartY=-101.683 StartZ=0 EndX=-12.1839 EndY=-100.177 EndZ=0
    g29: LineSegment StartX=-12.1839 StartY=-100.177 StartZ=0 EndX=-11.5268 EndY=-96.0291 EndZ=0
    g30: LineSegment StartX=-11.5268 StartY=-96.0291 StartZ=0 EndX=-14.7909 EndY=-93.3859 EndZ=0
    g31: Circle [constr] CenterX=-15.4479 CenterY=-97.5342 CenterZ=0 NormalX=0 NormalY=0 NormalZ=1 AngleXU=0 Radius=4.2
  constraints (70):
    c: Distance(g0) = 98.75
    c: Angle(g-1,g0) = 1.41372
    c: Coincident(g0,g-1)
    c: Coincident(g1,g2)
    c: Coincident(g2,g3)
    c: Coincident(g3,g4)
    c: Coincident(g4,g5)
    c: Coincident(g5,g6)
    c: Coincident(g6,g1)
    c: Equal(g1, g2-g6) x5
    c: PointOnObject(g1,g7)
    c: PointOnObject(g2,g7)
    c: PointOnObject(g3,g7)
    c: PointOnObject(g4,g7)
    c: PointOnObject(g5,g7)
    c: PointOnObject(g6,g7)
    c: Radius(g7) = 4.2
    c: Coincident(g7,g0)
    c: PointOnObject(g6,g0)
    c: Distance(g8) = 98.75
    c: Coincident(g9,g10)
    c: Coincident(g10,g11)
    c: Coincident(g11,g12)
    c: Coincident(g12,g13)
    c: Coincident(g13,g14)
    c: Coincident(g14,g9)
    c: Equal(g9, g10-g14) x5
    c: PointOnObject(g9,g15)
    c: PointOnObject(g10,g15)
    c: PointOnObject(g11,g15)
    c: PointOnObject(g12,g15)
    c: PointOnObject(g13,g15)
    c: PointOnObject(g14,g15)
    c: Radius(g15) = 4.2
    c: Coincident(g15,g8)
    c: PointOnObject(g14,g8)
    c: Distance(g16) = 98.75
    c: Coincident(g17,g18)
    c: Coincident(g18,g19)
    c: Coincident(g19,g20)
    c: Coincident(g20,g21)
    c: Coincident(g21,g22)
    c: Coincident(g22,g17)
    c: Equal(g17, g18-g22) x5
    c: PointOnObject(g17,g23)
    c: PointOnObject(g18,g23)
    c: PointOnObject(g19,g23)
    c: PointOnObject(g20,g23)
    c: PointOnObject(g21,g23)
    c: PointOnObject(g22,g23)
    c: Radius(g23) = 4.2
    c: Coincident(g23,g16)
    c: PointOnObject(g22,g16)
    c: Distance(g24) = 98.75
    c: Coincident(g25,g26)
    c: Coincident(g26,g27)
    c: Coincident(g27,g28)
    c: Coincident(g28,g29)
    c: Coincident(g29,g30)
    c: Coincident(g30,g25)
    c: Equal(g25, g26-g30) x5
    c: PointOnObject(g25,g31)
    c: PointOnObject(g26,g31)
    c: PointOnObject(g27,g31)
    c: PointOnObject(g28,g31)
    c: PointOnObject(g29,g31)
    c: PointOnObject(g30,g31)
    c: Radius(g31) = 4.2
    c: Coincident(g31,g24)
    c: PointOnObject(g30,g24)
FEATURE [PartDesign::Pocket] Pocket007
  BaseFeature = -> Pocket006
  Direction = (0,0,1)
  Length = 5
  Length2 = 5
  Profile = -> Sketch020
  ReferenceAxis = -> Sketch020 [N_Axis]
  Refine = true
  Suppressed = false
  Type = 0
FEATURE [PartDesign::Body] Body002  label="CaseA"
  AllowCompound = false
  Group = -> [Sketch002,Pad001,DatumPlane,Sketch005,Pocket,Sketch016,Pocket004,Chamfer001,Sketch017,Sketch018,Pocket005,Sketch019,Pocket006,Sketch020,Pocket007]
  Origin = -> Origin002
  Tip = -> Pocket007
FEATURE [Sketcher::SketchObject] Sketch021
  ArcFitTolerance = 1e-06
  AttachmentSupport = -> [XY_Plane006]
  FullyConstrained = true
  MakeInternals = false
  MapMode = 5
  sketch-geometry (2):
    g0: Circle CenterX=0 CenterY=0 CenterZ=0 NormalX=0 NormalY=0 NormalZ=1 AngleXU=0 Radius=115
    g1: Circle CenterX=0 CenterY=0 CenterZ=0 NormalX=0 NormalY=0 NormalZ=1 AngleXU=0 Radius=83.5
  constraints (4):
    c: Diameter(g0) = 230
    c: Coincident(g0,g-1)
    c: Diameter(g1) = 167
    c: Coincident(g1,g0)
FEATURE [PartDesign::Pad] Pad009
  Direction = (0,0,1)
  Length = 15
  Length2 = 10
  Profile = -> Sketch021
  ReferenceAxis = -> Sketch021 [N_Axis]
  Refine = true
  Suppressed = false
  Type = 0
FEATURE [Sketcher::SketchObject] Sketch022
  ArcFitTolerance = 1e-06
  AttachmentSupport = -> [Pad009]
  FullyConstrained = false
  MakeInternals = false
  MapMode = 5
  Placement = pos=(0,0,15) rot=(0,0,1;0rad)
  sketch-geometry (40):
    g0: LineSegment [constr] StartX=0 StartY=0 StartZ=0 EndX=44.0086 EndY=106.246 EndZ=0
    g1: LineSegment StartX=44.5568 StartY=70.6183 StartZ=0 EndX=61.3657 EndY=97.2587 EndZ=0
    g2: LineSegment StartX=18.4283 StartY=81.4411 StartZ=0 EndX=25.3802 EndY=112.164 EndZ=0
    g3: ArcOfCircle CenterX=-1.31235e-05 CenterY=-9.2e-15 CenterZ=0 NormalX=0 NormalY=0 NormalZ=1 AngleXU=0 Radius=115 StartAngle=1.00793 EndAngle=1.34827
    g4: ArcOfCircle CenterX=0 CenterY=0 CenterZ=0 NormalX=0 NormalY=0 NormalZ=1 AngleXU=0 Radius=83.5 StartAngle=1.00793 EndAngle=1.34827
    g5: LineSegment [constr] StartX=-1.31235e-05 StartY=-9.2e-15 StartZ=0 EndX=81.3173 EndY=81.3173 EndZ=0
    g6: LineSegment StartX=70.6183 StartY=44.5568 StartZ=0 EndX=97.2587 EndY=61.3657 EndZ=0
    g7: LineSegment StartX=81.4411 StartY=18.4282 StartZ=0 EndX=112.164 EndY=25.3802 EndZ=0
    g8: ArcOfCircle CenterX=-1.31235e-05 CenterY=-9.2e-15 CenterZ=0 NormalX=0 NormalY=0 NormalZ=1 AngleXU=0 Radius=115 StartAngle=0.22253 EndAngle=0.562869
    g9: ArcOfCircle CenterX=-1.31235e-05 CenterY=1.31235e-05 CenterZ=0 NormalX=0 NormalY=0 NormalZ=1 AngleXU=0 Radius=83.5 StartAngle=0.222529 EndAngle=0.562869
    g10: LineSegment [constr] StartX=0 StartY=0 StartZ=0 EndX=-44.0086 EndY=106.246 EndZ=0
    g11: LineSegment StartX=-44.5568 StartY=70.6183 StartZ=0 EndX=-61.3657 EndY=97.2587 EndZ=0
    g12: LineSegment StartX=-18.4283 StartY=81.4411 StartZ=0 EndX=-25.3802 EndY=112.164 EndZ=0
    g13: ArcOfCircle CenterX=1.31235e-05 CenterY=-9.2e-15 CenterZ=0 NormalX=0 NormalY=0 NormalZ=1 AngleXU=0 Radius=115 StartAngle=1.79333 EndAngle=2.13367
    g14: ArcOfCircle CenterX=0 CenterY=0 CenterZ=0 NormalX=0 NormalY=0 NormalZ=1 AngleXU=0 Radius=83.5 StartAngle=1.79333 EndAngle=2.13367
    g15: LineSegment [constr] StartX=1.31235e-05 StartY=-9.2e-15 StartZ=0 EndX=-81.3173 EndY=81.3173 EndZ=0
    g16: LineSegment StartX=-70.6183 StartY=44.5568 StartZ=0 EndX=-97.2587 EndY=61.3657 EndZ=0
    g17: LineSegment StartX=-81.4411 StartY=18.4282 StartZ=0 EndX=-112.164 EndY=25.3802 EndZ=0
    g18: ArcOfCircle CenterX=1.31235e-05 CenterY=-9.2e-15 CenterZ=0 NormalX=0 NormalY=0 NormalZ=1 AngleXU=0 Radius=115 StartAngle=2.57872 EndAngle=2.91906
    g19: ArcOfCircle CenterX=1.31235e-05 CenterY=1.31235e-05 CenterZ=0 NormalX=0 NormalY=0 NormalZ=1 AngleXU=0 Radius=83.5 StartAngle=2.57872 EndAngle=2.91906
    g20: LineSegment [constr] StartX=0 StartY=0 StartZ=0 EndX=44.0086 EndY=-106.246 EndZ=0
    g21: LineSegment StartX=44.5568 StartY=-70.6183 StartZ=0 EndX=61.3657 EndY=-97.2587 EndZ=0
    g22: LineSegment StartX=18.4283 StartY=-81.4411 StartZ=0 EndX=25.3802 EndY=-112.164 EndZ=0
    g23: ArcOfCircle CenterX=-1.31235e-05 CenterY=9.2e-15 CenterZ=0 NormalX=0 NormalY=0 NormalZ=1 AngleXU=0 Radius=115 StartAngle=4.93492 EndAngle=5.27526
    g24: ArcOfCircle CenterX=0 CenterY=0 CenterZ=0 NormalX=0 NormalY=0 NormalZ=1 AngleXU=0 Radius=83.5 StartAngle=4.93492 EndAngle=5.27526
    g25: LineSegment [constr] StartX=-1.31235e-05 StartY=9.2e-15 StartZ=0 EndX=81.3173 EndY=-81.3173 EndZ=0
    g26: LineSegment StartX=70.6183 StartY=-44.5568 StartZ=0 EndX=97.2587 EndY=-61.3657 EndZ=0
    g27: LineSegment StartX=81.4411 StartY=-18.4282 StartZ=0 EndX=112.164 EndY=-25.3802 EndZ=0
    g28: ArcOfCircle CenterX=-1.31235e-05 CenterY=9.2e-15 CenterZ=0 NormalX=0 NormalY=0 NormalZ=1 AngleXU=0 Radius=115 StartAngle=5.72032 EndAngle=6.06066
    g29: ArcOfCircle CenterX=-1.31235e-05 CenterY=-1.31235e-05 CenterZ=0 NormalX=0 NormalY=0 NormalZ=1 AngleXU=0 Radius=83.5 StartAngle=5.72032 EndAngle=6.06066
    g30: LineSegment [constr] StartX=0 StartY=0 StartZ=0 EndX=-44.0086 EndY=-106.246 EndZ=0
    g31: LineSegment StartX=-44.5568 StartY=-70.6183 StartZ=0 EndX=-61.3657 EndY=-97.2587 EndZ=0
    g32: LineSegment StartX=-18.4283 StartY=-81.4411 StartZ=0 EndX=-25.3802 EndY=-112.164 EndZ=0
    g33: ArcOfCircle CenterX=1.31235e-05 CenterY=9.2e-15 CenterZ=0 NormalX=0 NormalY=0 NormalZ=1 AngleXU=0 Radius=115 StartAngle=4.14952 EndAngle=4.48986
    g34: ArcOfCircle CenterX=0 CenterY=0 CenterZ=0 NormalX=0 NormalY=0 NormalZ=1 AngleXU=0 Radius=83.5 StartAngle=4.14952 EndAngle=4.48986
    g35: LineSegment [constr] StartX=1.31235e-05 StartY=9.2e-15 StartZ=0 EndX=-81.3173 EndY=-81.3173 EndZ=0
    g36: LineSegment StartX=-70.6183 StartY=-44.5568 StartZ=0 EndX=-97.2587 EndY=-61.3657 EndZ=0
    g37: LineSegment StartX=-81.4411 StartY=-18.4282 StartZ=0 EndX=-112.164 EndY=-25.3802 EndZ=0
    g38: ArcOfCircle CenterX=1.31235e-05 CenterY=9.2e-15 CenterZ=0 NormalX=0 NormalY=0 NormalZ=1 AngleXU=0 Radius=115 StartAngle=3.36412 EndAngle=3.70446
    g39: ArcOfCircle CenterX=1.31235e-05 CenterY=-1.31235e-05 CenterZ=0 NormalX=0 NormalY=0 NormalZ=1 AngleXU=0 Radius=83.5 StartAngle=3.36412 EndAngle=3.70446
  constraints (70):
    c: Distance(g0) = 115
    c: Coincident(g0,g-1)
    c: Angle(g1,g0) = 0.17017
    c: PointOnObject(g0,g3)
    c: Diameter(g4) = 167
    c: Coincident(g4,g0)
    c: Coincident(g3,g2)
    c: Coincident(g3,g1)
    c: Angle(g0,g2) = 0.17017
    c: Coincident(g1,g4)
    c: Coincident(g2,g4)
    c: Distance(g5) = 115
    c: Angle(g-1,g5) = 0.785398
    c: Coincident(g5,g3)
    c: Diameter(g9) = 167
    c: Coincident(g8,g7)
    c: Coincident(g8,g6)
    c: Coincident(g6,g9)
    c: Coincident(g7,g9)
    c: Distance(g10) = 115
    c: Angle(g11,g10) = -0.17017
    c: PointOnObject(g10,g13)
    c: Diameter(g14) = 167
    c: Coincident(g14,g10)
    c: Coincident(g13,g12)
    c: Coincident(g13,g11)
    c: Angle(g10,g12) = -0.17017
    c: Coincident(g11,g14)
    c: Coincident(g12,g14)
    c: Distance(g15) = 115
    c: Coincident(g15,g13)
    c: Diameter(g19) = 167
    c: Coincident(g18,g17)
    c: Coincident(g18,g16)
    c: Coincident(g16,g19)
    c: Coincident(g17,g19)
    c: Distance(g20) = 115
    c: Angle(g21,g20) = -0.17017
    c: PointOnObject(g20,g23)
    c: Diameter(g24) = 167
    c: Coincident(g24,g20)
    c: Coincident(g23,g22)
    c: Coincident(g23,g21)
    c: Angle(g20,g22) = -0.17017
    c: Coincident(g21,g24)
    c: Coincident(g22,g24)
    c: Distance(g25) = 115
    c: Coincident(g25,g23)
    c: Diameter(g29) = 167
    c: Coincident(g28,g27)
    c: Coincident(g28,g26)
    c: Coincident(g26,g29)
    c: Coincident(g27,g29)
    c: Distance(g30) = 115
    c: Angle(g31,g30) = 0.17017
    c: PointOnObject(g30,g33)
    c: Diameter(g34) = 167
    c: Coincident(g34,g30)
    c: Coincident(g33,g32)
    c: Coincident(g33,g31)
    c: Angle(g30,g32) = 0.17017
    c: Coincident(g31,g34)
    c: Coincident(g32,g34)
    c: Distance(g35) = 115
    c: Coincident(g35,g33)
    c: Diameter(g39) = 167
    c: Coincident(g38,g37)
    c: Coincident(g38,g36)
    c: Coincident(g36,g39)
    c: Coincident(g37,g39)
FEATURE [PartDesign::Pocket] Pocket008
  BaseFeature = -> Pad009
  Direction = (0,0,-1)
  Length = 10
  Length2 = 5
  Profile = -> Sketch022
  ReferenceAxis = -> Sketch022 [N_Axis]
  Refine = true
  Suppressed = false
  Type = 0
FEATURE [Sketcher::SketchObject] Sketch023
  ArcFitTolerance = 1e-06
  AttachmentSupport = -> [Pocket008]
  FullyConstrained = true
  MakeInternals = false
  MapMode = 5
  Placement = pos=(0,0,0) rot=(1,0,0;3.14159rad)
  sketch-geometry (2):
    g0: Circle CenterX=0 CenterY=0 CenterZ=0 NormalX=0 NormalY=0 NormalZ=1 AngleXU=0 Radius=85.5
    g1: Circle CenterX=0 CenterY=0 CenterZ=0 NormalX=0 NormalY=0 NormalZ=1 AngleXU=0 Radius=113
  constraints (4):
    c: Diameter(g0) = 171
    c: Coincident(g0,g-1)
    c: Diameter(g1) = 226
    c: Coincident(g1,g0)
FEATURE [PartDesign::Pocket] Pocket009
  BaseFeature = -> Pocket008
  Direction = (0,0,1)
  Length = 10
  Length2 = 5
  Profile = -> Sketch023
  ReferenceAxis = -> Sketch023 [N_Axis]
  Refine = true
  Suppressed = false
  Type = 0
FEATURE [Sketcher::SketchObject] Sketch024
  ArcFitTolerance = 1e-06
  AttachmentSupport = -> [Pocket009]
  FullyConstrained = false
  MakeInternals = false
  MapMode = 5
  Placement = pos=(0,0,5) rot=(0,0,1;0rad)
  sketch-geometry (6):
    g0: LineSegment [constr] StartX=0 StartY=0 StartZ=0 EndX=44.0086 EndY=106.246 EndZ=0
    g1: LineSegment StartX=46.6575 StartY=99.69 StartZ=0 EndX=50.5648 EndY=108.895 EndZ=0
    g2: LineSegment StartX=50.5648 StartY=108.895 StartZ=0 EndX=41.3598 EndY=112.802 EndZ=0
    g3: LineSegment StartX=41.3598 StartY=112.802 StartZ=0 EndX=37.4524 EndY=103.597 EndZ=0
    g4: LineSegment StartX=37.4524 StartY=103.597 StartZ=0 EndX=46.6575 EndY=99.69 EndZ=0
    g5: GeomPoint [constr] X=44.0086 Y=106.246 Z=0
  constraints (10):
    c: Distance(g0) = 115
    c: Angle(g-1,g0) = 1.1781
    c: Coincident(g0,g-1)
    c: Coincident(g1,g2)
    c: Coincident(g2,g3)
    c: Coincident(g3,g4)
    c: Coincident(g4,g1)
    c: Symmetric(g3,g1,g5)
    c: Distance(g2,g4) = 10
    c: Distance(g1,g3) = 10
FEATURE [Sketcher::SketchObject] Sketch025
  ArcFitTolerance = 1e-06
  AttachmentSupport = -> [Pad009]
  FullyConstrained = false
  MakeInternals = false
  MapMode = 5
  Placement = pos=(0,0,15) rot=(0,0,1;0rad)
  sketch-geometry (22):
    g0: LineSegment [constr] StartX=0 StartY=0 StartZ=0 EndX=81.3173 EndY=81.3173 EndZ=0
    g1: LineSegment [constr] StartX=0 StartY=0 StartZ=0 EndX=58.0438 EndY=79.8904 EndZ=0
    g2: Circle CenterX=58.0438 CenterY=79.8904 CenterZ=0 NormalX=0 NormalY=0 NormalZ=1 AngleXU=0 Radius=3.5
    g3: LineSegment [constr] StartX=0 StartY=0 StartZ=0 EndX=15.4479 EndY=97.5342 EndZ=0
    g4: Circle CenterX=15.4479 CenterY=97.5342 CenterZ=0 NormalX=0 NormalY=0 NormalZ=1 AngleXU=0 Radius=3.5
    g5: Circle CenterX=79.8905 CenterY=58.0438 CenterZ=0 NormalX=0 NormalY=0 NormalZ=1 AngleXU=0 Radius=3.5
    g6: Circle CenterX=97.5342 CenterY=15.4478 CenterZ=0 NormalX=0 NormalY=0 NormalZ=1 AngleXU=0 Radius=3.5
    g7: Circle CenterX=58.0438 CenterY=-79.8904 CenterZ=0 NormalX=0 NormalY=0 NormalZ=1 AngleXU=0 Radius=3.5
    g8: Circle CenterX=15.4479 CenterY=-97.5342 CenterZ=0 NormalX=0 NormalY=0 NormalZ=1 AngleXU=0 Radius=3.5
    g9: Circle CenterX=79.8905 CenterY=-58.0438 CenterZ=0 NormalX=0 NormalY=0 NormalZ=1 AngleXU=0 Radius=3.5
    g10: Circle CenterX=97.5342 CenterY=-15.4478 CenterZ=0 NormalX=0 NormalY=0 NormalZ=1 AngleXU=0 Radius=3.5
    g11: LineSegment [constr] StartX=0 StartY=0 StartZ=0 EndX=-81.3173 EndY=81.3173 EndZ=0
    g12: LineSegment [constr] StartX=0 StartY=0 StartZ=0 EndX=-58.0438 EndY=79.8904 EndZ=0
    g13: Circle CenterX=-58.0438 CenterY=79.8904 CenterZ=0 NormalX=0 NormalY=0 NormalZ=1 AngleXU=0 Radius=3.5
    g14: LineSegment [constr] StartX=0 StartY=0 StartZ=0 EndX=-15.4479 EndY=97.5342 EndZ=0
    g15: Circle CenterX=-15.4479 CenterY=97.5342 CenterZ=0 NormalX=0 NormalY=0 NormalZ=1 AngleXU=0 Radius=3.5
    g16: Circle CenterX=-79.8905 CenterY=58.0438 CenterZ=0 NormalX=0 NormalY=0 NormalZ=1 AngleXU=0 Radius=3.5
    g17: Circle CenterX=-97.5342 CenterY=15.4478 CenterZ=0 NormalX=0 NormalY=0 NormalZ=1 AngleXU=0 Radius=3.5
    g18: Circle CenterX=-58.0438 CenterY=-79.8904 CenterZ=0 NormalX=0 NormalY=0 NormalZ=1 AngleXU=0 Radius=3.5
    g19: Circle CenterX=-15.4479 CenterY=-97.5342 CenterZ=0 NormalX=0 NormalY=0 NormalZ=1 AngleXU=0 Radius=3.5
    g20: Circle CenterX=-79.8905 CenterY=-58.0438 CenterZ=0 NormalX=0 NormalY=0 NormalZ=1 AngleXU=0 Radius=3.5
    g21: Circle CenterX=-97.5342 CenterY=-15.4478 CenterZ=0 NormalX=0 NormalY=0 NormalZ=1 AngleXU=0 Radius=3.5
  constraints (34):
    c: Distance(g0) = 115
    c: Angle(g-1,g0) = 0.785398
    c: Coincident(g0,g-1)
    c: Distance(g1) = 98.75
    c: Angle(g-1,g1) = 0.942478
    c: Coincident(g1,g0)
    c: Diameter(g2) = 7
    c: Coincident(g2,g1)
    c: Distance(g3) = 98.75
    c: Angle(g-1,g3) = 1.41372
    c: Coincident(g3,g0)
    c: Diameter(g4) = 7
    c: Coincident(g4,g3)
    c: Diameter(g5) = 7
    c: Diameter(g6) = 7
    c: Diameter(g7) = 7
    c: Diameter(g8) = 7
    c: Diameter(g9) = 7
    c: Diameter(g10) = 7
    c: Distance(g11) = 115
    c: Distance(g12) = 98.75
    c: Coincident(g12,g11)
    c: Diameter(g13) = 7
    c: Coincident(g13,g12)
    c: Distance(g14) = 98.75
    c: Coincident(g14,g11)
    c: Diameter(g15) = 7
    c: Coincident(g15,g14)
    c: Diameter(g16) = 7
    c: Diameter(g17) = 7
    c: Diameter(g18) = 7
    c: Diameter(g19) = 7
    c: Diameter(g20) = 7
    c: Diameter(g21) = 7
FEATURE [PartDesign::Pocket] Pocket010
  BaseFeature = -> Pocket009
  Direction = (0,0,-1)
  Length = 5
  Length2 = 5
  Profile = -> Sketch024
  ReferenceAxis = -> Sketch024 [N_Axis]
  Refine = true
  Suppressed = false
  Type = 0
FEATURE [PartDesign::Pocket] Pocket011
  BaseFeature = -> Pocket010
  Direction = (0,0,-1)
  Length = 2
  Length2 = 5
  Profile = -> Sketch025
  ReferenceAxis = -> Sketch025 [N_Axis]
  Refine = true
  Suppressed = false
  Type = 0
FEATURE [Sketcher::SketchObject] Sketch026
  ArcFitTolerance = 1e-06
  AttachmentSupport = -> [Pocket011]
  FullyConstrained = true
  MakeInternals = false
  MapMode = 5
  Placement = pos=(0,0,10) rot=(1,0,0;3.14159rad)
FEATURE [Sketcher::SketchObject] Sketch027
  ArcFitTolerance = 1e-06
  AttachmentSupport = -> [Pocket011]
  FullyConstrained = true
  MakeInternals = false
  MapMode = 5
  Placement = pos=(0,0,10) rot=(1,0,0;3.14159rad)
  sketch-geometry (4):
    g0: LineSegment [constr] StartX=0 StartY=0 StartZ=0 EndX=-15.4479 EndY=97.5342 EndZ=0
    g1: Circle CenterX=-15.4479 CenterY=97.5342 CenterZ=0 NormalX=0 NormalY=0 NormalZ=1 AngleXU=0 Radius=2.5
    g2: LineSegment [constr] StartX=0 StartY=0 StartZ=0 EndX=15.4479 EndY=97.5342 EndZ=0
    g3: Circle CenterX=15.4479 CenterY=97.5342 CenterZ=0 NormalX=0 NormalY=0 NormalZ=1 AngleXU=0 Radius=2.5
  constraints (10):
    c: Distance(g0) = 98.75
    c: Angle(g-1,g0) = 1.72788
    c: Coincident(g0,g-1)
    c: Diameter(g1) = 5
    c: Coincident(g1,g0)
    c: Distance(g2) = 98.75
    c: Angle(g-1,g2) = 1.41372
    c: Coincident(g2,g-1)
    c: Diameter(g3) = 5
    c: Coincident(g3,g2)
FEATURE [PartDesign::Pad] Pad010
  BaseFeature = -> Pocket011
  Direction = (0,0,-1)
  Length = 5.4
  Length2 = 10
  Profile = -> Sketch027
  ReferenceAxis = -> Sketch027 [N_Axis]
  Refine = true
  Suppressed = false
  Type = 0
FEATURE [Sketcher::SketchObject] Sketch028
  ArcFitTolerance = 1e-06
  AttachmentSupport = -> [Pad010]
  FullyConstrained = true
  MakeInternals = false
  MapMode = 5
  Placement = pos=(0,0,10) rot=(1,0,0;3.14159rad)
  sketch-geometry (5):
    g0: LineSegment [constr] StartX=0 StartY=0 StartZ=0 EndX=58.0438 EndY=79.8904 EndZ=0
    g1: Circle CenterX=58.0438 CenterY=79.8904 CenterZ=0 NormalX=0 NormalY=0 NormalZ=1 AngleXU=0 Radius=2.5
    g2: LineSegment [constr] StartX=0 StartY=0 StartZ=0 EndX=79.8904 EndY=58.0438 EndZ=0
    g3: Circle CenterX=79.8904 CenterY=58.0438 CenterZ=0 NormalX=0 NormalY=0 NormalZ=1 AngleXU=0 Radius=2.5
    g4: LineSegment [constr] StartX=0 StartY=0 StartZ=0 EndX=81.3173 EndY=81.3173 EndZ=0
  constraints (13):
    c: Distance(g0) = 98.75
    c: Coincident(g0,g-1)
    c: Diameter(g1) = 5
    c: Coincident(g1,g0)
    c: Distance(g2) = 98.75
    c: Coincident(g2,g-1)
    c: Diameter(g3) = 5
    c: Coincident(g3,g2)
    c: Distance(g4) = 115
    c: Coincident(g4,g0)
    c: Angle(g2,g4) = 0.15708
    c: Angle(g4,g0) = 0.15708
    c: Angle(g-1,g4) = 0.785398
FEATURE [PartDesign::Pad] Pad011
  BaseFeature = -> Pad010
  Direction = (0,0,-1)
  Length = 5.4
  Length2 = 10
  Profile = -> Sketch028
  ReferenceAxis = -> Sketch028 [N_Axis]
  Refine = true
  Suppressed = false
  Type = 0
FEATURE [Sketcher::SketchObject] Sketch029
  ArcFitTolerance = 1e-06
  AttachmentSupport = -> [Pad011]
  FullyConstrained = true
  MakeInternals = false
  MapMode = 5
  Placement = pos=(0,0,10) rot=(1,0,0;3.14159rad)
  sketch-geometry (5):
    g0: LineSegment [constr] StartX=0 StartY=0 StartZ=0 EndX=97.5342 EndY=15.4479 EndZ=0
    g1: Circle CenterX=97.5342 CenterY=15.4479 CenterZ=0 NormalX=0 NormalY=0 NormalZ=1 AngleXU=0 Radius=2.5
    g2: LineSegment [constr] StartX=0 StartY=0 StartZ=0 EndX=97.5342 EndY=-15.4479 EndZ=0
    g3: Circle CenterX=97.5342 CenterY=-15.4479 CenterZ=0 NormalX=0 NormalY=0 NormalZ=1 AngleXU=0 Radius=2.5
    g4: LineSegment [constr] StartX=0 StartY=0 StartZ=0 EndX=115 EndY=0 EndZ=0
  constraints (13):
    c: Distance(g0) = 98.75
    c: Coincident(g0,g-1)
    c: Diameter(g1) = 5
    c: Coincident(g1,g0)
    c: Distance(g2) = 98.75
    c: Coincident(g2,g-1)
    c: Diameter(g3) = 5
    c: Coincident(g3,g2)
    c: Distance(g4) = 115
    c: Coincident(g4,g0)
    c: Angle(g2,g4) = 0.15708
    c: Angle(g4,g0) = 0.15708
    c: Angle(g-1,g4) = 0
FEATURE [PartDesign::Pad] Pad012
  BaseFeature = -> Pad011
  Direction = (0,0,-1)
  Length = 5.4
  Length2 = 10
  Profile = -> Sketch029
  ReferenceAxis = -> Sketch029 [N_Axis]
  Refine = true
  Suppressed = false
  Type = 0
FEATURE [Sketcher::SketchObject] Sketch030
  ArcFitTolerance = 1e-06
  AttachmentSupport = -> [Pad012]
  FullyConstrained = true
  MakeInternals = false
  MapMode = 5
  Placement = pos=(0,0,10) rot=(1,0,0;3.14159rad)
  sketch-geometry (5):
    g0: LineSegment [constr] StartX=0 StartY=0 StartZ=0 EndX=79.8904 EndY=-58.0438 EndZ=0
    g1: Circle CenterX=79.8904 CenterY=-58.0438 CenterZ=0 NormalX=0 NormalY=0 NormalZ=1 AngleXU=0 Radius=2.5
    g2: LineSegment [constr] StartX=0 StartY=0 StartZ=0 EndX=58.0438 EndY=-79.8904 EndZ=0
    g3: Circle CenterX=58.0438 CenterY=-79.8904 CenterZ=0 NormalX=0 NormalY=0 NormalZ=1 AngleXU=0 Radius=2.5
    g4: LineSegment [constr] StartX=0 StartY=0 StartZ=0 EndX=81.3173 EndY=-81.3173 EndZ=0
  constraints (13):
    c: Distance(g0) = 98.75
    c: Coincident(g0,g-1)
    c: Diameter(g1) = 5
    c: Coincident(g1,g0)
    c: Distance(g2) = 98.75
    c: Coincident(g2,g-1)
    c: Diameter(g3) = 5
    c: Coincident(g3,g2)
    c: Distance(g4) = 115
    c: Coincident(g4,g0)
    c: Angle(g2,g4) = 0.15708
    c: Angle(g4,g0) = 0.15708
    c: Angle(g-1,g4) = -0.785398
FEATURE [PartDesign::Pad] Pad013
  BaseFeature = -> Pad012
  Direction = (0,0,-1)
  Length = 5.4
  Length2 = 10
  Profile = -> Sketch030
  ReferenceAxis = -> Sketch030 [N_Axis]
  Refine = true
  Suppressed = false
  Type = 0
FEATURE [Sketcher::SketchObject] Sketch031
  ArcFitTolerance = 1e-06
  AttachmentSupport = -> [Pad013]
  FullyConstrained = true
  MakeInternals = false
  MapMode = 5
  Placement = pos=(0,0,10) rot=(1,0,0;3.14159rad)
  sketch-geometry (5):
    g0: LineSegment [constr] StartX=0 StartY=0 StartZ=0 EndX=15.4479 EndY=-97.5342 EndZ=0
    g1: Circle CenterX=15.4479 CenterY=-97.5342 CenterZ=0 NormalX=0 NormalY=0 NormalZ=1 AngleXU=0 Radius=2.5
    g2: LineSegment [constr] StartX=0 StartY=0 StartZ=0 EndX=-15.4479 EndY=-97.5342 EndZ=0
    g3: Circle CenterX=-15.4479 CenterY=-97.5342 CenterZ=0 NormalX=0 NormalY=0 NormalZ=1 AngleXU=0 Radius=2.5
    g4: LineSegment [constr] StartX=0 StartY=0 StartZ=0 EndX=-2.2e-15 EndY=-115 EndZ=0
  constraints (13):
    c: Distance(g0) = 98.75
    c: Coincident(g0,g-1)
    c: Diameter(g1) = 5
    c: Coincident(g1,g0)
    c: Distance(g2) = 98.75
    c: Coincident(g2,g-1)
    c: Diameter(g3) = 5
    c: Coincident(g3,g2)
    c: Distance(g4) = 115
    c: Coincident(g4,g0)
    c: Angle(g2,g4) = 0.15708
    c: Angle(g4,g0) = 0.15708
    c: Angle(g-1,g4) = -1.5708
FEATURE [PartDesign::Pad] Pad014
  BaseFeature = -> Pad013
  Direction = (0,0,-1)
  Length = 5.4
  Length2 = 10
  Profile = -> Sketch031
  ReferenceAxis = -> Sketch031 [N_Axis]
  Refine = true
  Suppressed = false
  Type = 0
FEATURE [Sketcher::SketchObject] Sketch032
  ArcFitTolerance = 1e-06
  AttachmentSupport = -> [Pad014]
  FullyConstrained = true
  MakeInternals = false
  MapMode = 5
  Placement = pos=(0,0,10) rot=(1,0,0;3.14159rad)
  sketch-geometry (5):
    g0: LineSegment [constr] StartX=0 StartY=0 StartZ=0 EndX=-58.0438 EndY=-79.8904 EndZ=0
    g1: Circle CenterX=-58.0438 CenterY=-79.8904 CenterZ=0 NormalX=0 NormalY=0 NormalZ=1 AngleXU=0 Radius=2.5
    g2: LineSegment [constr] StartX=0 StartY=0 StartZ=0 EndX=-79.8904 EndY=-58.0438 EndZ=0
    g3: Circle CenterX=-79.8904 CenterY=-58.0438 CenterZ=0 NormalX=0 NormalY=0 NormalZ=1 AngleXU=0 Radius=2.5
    g4: LineSegment [constr] StartX=0 StartY=0 StartZ=0 EndX=-81.3173 EndY=-81.3173 EndZ=0
  constraints (13):
    c: Distance(g0) = 98.75
    c: Coincident(g0,g-1)
    c: Diameter(g1) = 5
    c: Coincident(g1,g0)
    c: Distance(g2) = 98.75
    c: Coincident(g2,g-1)
    c: Diameter(g3) = 5
    c: Coincident(g3,g2)
    c: Distance(g4) = 115
    c: Coincident(g4,g0)
    c: Angle(g2,g4) = 0.15708
    c: Angle(g4,g0) = 0.15708
    c: Angle(g-1,g4) = 3.92699
FEATURE [PartDesign::Pad] Pad015
  BaseFeature = -> Pad014
  Direction = (0,0,-1)
  Length = 5.4
  Length2 = 10
  Profile = -> Sketch032
  ReferenceAxis = -> Sketch032 [N_Axis]
  Refine = true
  Suppressed = false
  Type = 0
FEATURE [Sketcher::SketchObject] Sketch033
  ArcFitTolerance = 1e-06
  AttachmentSupport = -> [Pad015]
  FullyConstrained = true
  MakeInternals = false
  MapMode = 5
  Placement = pos=(0,0,10) rot=(1,0,0;3.14159rad)
  sketch-geometry (5):
    g0: LineSegment [constr] StartX=0 StartY=0 StartZ=0 EndX=-97.5342 EndY=-15.4479 EndZ=0
    g1: Circle CenterX=-97.5342 CenterY=-15.4479 CenterZ=0 NormalX=0 NormalY=0 NormalZ=1 AngleXU=0 Radius=2.5
    g2: LineSegment [constr] StartX=0 StartY=0 StartZ=0 EndX=-97.5342 EndY=15.4479 EndZ=0
    g3: Circle CenterX=-97.5342 CenterY=15.4479 CenterZ=0 NormalX=0 NormalY=0 NormalZ=1 AngleXU=0 Radius=2.5
    g4: LineSegment [constr] StartX=0 StartY=0 StartZ=0 EndX=-115 EndY=1.1e-14 EndZ=0
  constraints (13):
    c: Distance(g0) = 98.75
    c: Coincident(g0,g-1)
    c: Diameter(g1) = 5
    c: Coincident(g1,g0)
    c: Distance(g2) = 98.75
    c: Coincident(g2,g-1)
    c: Diameter(g3) = 5
    c: Coincident(g3,g2)
    c: Distance(g4) = 115
    c: Coincident(g4,g0)
    c: Angle(g2,g4) = 0.15708
    c: Angle(g4,g0) = 0.15708
    c: Angle(g-1,g4) = 3.14159
FEATURE [PartDesign::Pad] Pad016
  BaseFeature = -> Pad015
  Direction = (0,0,-1)
  Length = 5.4
  Length2 = 10
  Profile = -> Sketch033
  ReferenceAxis = -> Sketch033 [N_Axis]
  Refine = true
  Suppressed = false
  Type = 0
FEATURE [Sketcher::SketchObject] Sketch034
  ArcFitTolerance = 1e-06
  AttachmentSupport = -> [Pad016]
  FullyConstrained = true
  MakeInternals = false
  MapMode = 5
  Placement = pos=(0,0,10) rot=(1,0,0;3.14159rad)
  sketch-geometry (5):
    g0: LineSegment [constr] StartX=0 StartY=0 StartZ=0 EndX=-79.8904 EndY=58.0438 EndZ=0
    g1: Circle CenterX=-79.8904 CenterY=58.0438 CenterZ=0 NormalX=0 NormalY=0 NormalZ=1 AngleXU=0 Radius=2.5
    g2: LineSegment [constr] StartX=0 StartY=0 StartZ=0 EndX=-58.0438 EndY=79.8904 EndZ=0
    g3: Circle CenterX=-58.0438 CenterY=79.8904 CenterZ=0 NormalX=0 NormalY=0 NormalZ=1 AngleXU=0 Radius=2.5
    g4: LineSegment [constr] StartX=0 StartY=0 StartZ=0 EndX=-81.3173 EndY=81.3173 EndZ=0
  constraints (13):
    c: Distance(g0) = 98.75
    c: Coincident(g0,g-1)
    c: Diameter(g1) = 5
    c: Coincident(g1,g0)
    c: Distance(g2) = 98.75
    c: Coincident(g2,g-1)
    c: Diameter(g3) = 5
    c: Coincident(g3,g2)
    c: Distance(g4) = 115
    c: Coincident(g4,g0)
    c: Angle(g2,g4) = 0.15708
    c: Angle(g4,g0) = 0.15708
    c: Angle(g-1,g4) = 2.35619
FEATURE [PartDesign::Pad] Pad017
  BaseFeature = -> Pad016
  Direction = (0,0,-1)
  Length = 5.4
  Length2 = 10
  Profile = -> Sketch034
  ReferenceAxis = -> Sketch034 [N_Axis]
  Refine = true
  Suppressed = false
  Type = 0
FEATURE [PartDesign::Chamfer] Chamfer002
  Angle = 45
  Base = -> Pad017 [Edge79,Edge97,Edge115,Edge133,Edge151,Edge178,Edge41,Edge43,Edge61]
  BaseFeature = -> Pad017
  ChamferType = 0
  FlipDirection = false
  Refine = true
  Size = 4
  Size2 = 1
  SupportTransform = false
  Suppressed = false
  UseAllEdges = false
FEATURE [PartDesign::Plane] DatumPlane001
  AttachmentSupport = -> [Chamfer002]
  Length = 275.873
  MapMode = 5
  Placement = pos=(0,0,13) rot=(0,0,1;0rad)
  ResizeMode = 0
  Width = 275.863
FEATURE [Sketcher::SketchObject] Sketch035
  ArcFitTolerance = 1e-06
  AttachmentSupport = -> [DatumPlane001]
  FullyConstrained = false
  MakeInternals = false
  MapMode = 5
  Placement = pos=(0,0,13) rot=(0,0,1;0rad)
  sketch-geometry (28):
    g0: LineSegment [constr] StartX=0 StartY=0 StartZ=0 EndX=58.0438 EndY=79.8904 EndZ=0
    g1: Circle CenterX=58.0438 CenterY=79.8904 CenterZ=0 NormalX=0 NormalY=0 NormalZ=1 AngleXU=0 Radius=2.1
    g2: LineSegment [constr] StartX=0 StartY=0 StartZ=0 EndX=15.4479 EndY=97.5342 EndZ=0
    g3: Circle CenterX=15.4479 CenterY=97.5342 CenterZ=0 NormalX=0 NormalY=0 NormalZ=1 AngleXU=0 Radius=2.1
    g4: LineSegment [constr] StartX=0 StartY=0 StartZ=0 EndX=81.3173 EndY=81.3173 EndZ=0
    g5: Circle CenterX=79.8905 CenterY=58.0438 CenterZ=0 NormalX=0 NormalY=0 NormalZ=1 AngleXU=0 Radius=2.1
    g6: Circle CenterX=97.5342 CenterY=15.4479 CenterZ=0 NormalX=0 NormalY=0 NormalZ=1 AngleXU=0 Radius=2.1
    g7: LineSegment [constr] StartX=0 StartY=0 StartZ=0 EndX=-58.0438 EndY=79.8904 EndZ=0
    g8: Circle CenterX=-58.0438 CenterY=79.8904 CenterZ=0 NormalX=0 NormalY=0 NormalZ=1 AngleXU=0 Radius=2.1
    g9: LineSegment [constr] StartX=0 StartY=0 StartZ=0 EndX=-15.4479 EndY=97.5342 EndZ=0
    g10: Circle CenterX=-15.4479 CenterY=97.5342 CenterZ=0 NormalX=0 NormalY=0 NormalZ=1 AngleXU=0 Radius=2.1
    g11: LineSegment [constr] StartX=0 StartY=0 StartZ=0 EndX=-81.3173 EndY=81.3173 EndZ=0
    g12: Circle CenterX=-79.8905 CenterY=58.0438 CenterZ=0 NormalX=0 NormalY=0 NormalZ=1 AngleXU=0 Radius=2.1
    g13: Circle CenterX=-97.5342 CenterY=15.4479 CenterZ=0 NormalX=0 NormalY=0 NormalZ=1 AngleXU=0 Radius=2.1
    g14: LineSegment [constr] StartX=0 StartY=0 StartZ=0 EndX=58.0438 EndY=-79.8904 EndZ=0
    g15: Circle CenterX=58.0438 CenterY=-79.8904 CenterZ=0 NormalX=0 NormalY=0 NormalZ=1 AngleXU=0 Radius=2.1
    g16: LineSegment [constr] StartX=0 StartY=0 StartZ=0 EndX=15.4479 EndY=-97.5342 EndZ=0
    g17: Circle CenterX=15.4479 CenterY=-97.5342 CenterZ=0 NormalX=0 NormalY=0 NormalZ=1 AngleXU=0 Radius=2.1
    g18: LineSegment [constr] StartX=0 StartY=0 StartZ=0 EndX=81.3173 EndY=-81.3173 EndZ=0
    g19: Circle CenterX=79.8905 CenterY=-58.0438 CenterZ=0 NormalX=0 NormalY=0 NormalZ=1 AngleXU=0 Radius=2.1
    g20: Circle CenterX=97.5342 CenterY=-15.4479 CenterZ=0 NormalX=0 NormalY=0 NormalZ=1 AngleXU=0 Radius=2.1
    g21: LineSegment [constr] StartX=0 StartY=0 StartZ=0 EndX=-58.0438 EndY=-79.8904 EndZ=0
    g22: Circle CenterX=-58.0438 CenterY=-79.8904 CenterZ=0 NormalX=0 NormalY=0 NormalZ=1 AngleXU=0 Radius=2.1
    g23: LineSegment [constr] StartX=0 StartY=0 StartZ=0 EndX=-15.4479 EndY=-97.5342 EndZ=0
    g24: Circle CenterX=-15.4479 CenterY=-97.5342 CenterZ=0 NormalX=0 NormalY=0 NormalZ=1 AngleXU=0 Radius=2.1
    g25: LineSegment [constr] StartX=0 StartY=0 StartZ=0 EndX=-81.3173 EndY=-81.3173 EndZ=0
    g26: Circle CenterX=-79.8905 CenterY=-58.0438 CenterZ=0 NormalX=0 NormalY=0 NormalZ=1 AngleXU=0 Radius=2.1
    g27: Circle CenterX=-97.5342 CenterY=-15.4479 CenterZ=0 NormalX=0 NormalY=0 NormalZ=1 AngleXU=0 Radius=2.1
  constraints (48):
    c: Distance(g0) = 98.75
    c: Coincident(g0,g-1)
    c: Diameter(g1) = 4.2
    c: Coincident(g1,g0)
    c: Distance(g2) = 98.75
    c: Coincident(g2,g-1)
    c: Diameter(g3) = 4.2
    c: Coincident(g3,g2)
    c: Distance(g4) = 115
    c: Coincident(g4,g0)
    c: Angle(g4,g0) = 0.15708
    c: Angle(g-1,g4) = 0.785398
    c: Angle(g2,g-2) = 0.15708
    c: Diameter(g5) = 4.2
    c: Diameter(g6) = 4.2
    c: Distance(g7) = 98.75
    c: Diameter(g8) = 4.2
    c: Coincident(g8,g7)
    c: Distance(g9) = 98.75
    c: Diameter(g10) = 4.2
    c: Coincident(g10,g9)
    c: Distance(g11) = 115
    c: Coincident(g11,g7)
    c: Angle(g11,g7) = -0.15708
    c: Diameter(g12) = 4.2
    c: Diameter(g13) = 4.2
    c: Distance(g14) = 98.75
    c: Diameter(g15) = 4.2
    c: Coincident(g15,g14)
    c: Distance(g16) = 98.75
    c: Diameter(g17) = 4.2
    c: Coincident(g17,g16)
    c: Distance(g18) = 115
    c: Coincident(g18,g14)
    c: Angle(g18,g14) = -0.15708
    c: Diameter(g19) = 4.2
    c: Diameter(g20) = 4.2
    c: Distance(g21) = 98.75
    c: Diameter(g22) = 4.2
    c: Coincident(g22,g21)
    c: Distance(g23) = 98.75
    c: Diameter(g24) = 4.2
    c: Coincident(g24,g23)
    c: Distance(g25) = 115
    c: Coincident(g25,g21)
    c: Angle(g25,g21) = 0.15708
    c: Diameter(g26) = 4.2
    c: Diameter(g27) = 4.2
FEATURE [PartDesign::Pocket] Pocket012
  BaseFeature = -> Chamfer002
  Direction = (0,0,-1)
  Length = 15
  Length2 = 5
  Profile = -> Sketch035
  ReferenceAxis = -> Sketch035 [N_Axis]
  Refine = true
  Suppressed = false
  Type = 0
FEATURE [Sketcher::SketchObject] Sketch036
  ArcFitTolerance = 1e-06
  AttachmentSupport = -> [Pad008]
  FullyConstrained = false
  MakeInternals = false
  MapMode = 5
  Placement = pos=(0,0,0) rot=(1,0,0;3.14159rad)
  sketch-geometry (132):
    g0: ArcOfCircle [constr] CenterX=-0.20211 CenterY=0.215301 CenterZ=0 NormalX=0 NormalY=0 NormalZ=1 AngleXU=0 Radius=98.75 StartAngle=6.28101 EndAngle=7.85193
    g1: LineSegment [constr] StartX=0 StartY=-0.03476 StartZ=0 EndX=97.3753 EndY=15.388 EndZ=0
    g2: LineSegment [constr] StartX=0 StartY=3.12475e-07 StartZ=0 EndX=79.8601 EndY=58.0219 EndZ=0
    g3: LineSegment [constr] StartX=-0.011779 StartY=0 StartZ=0 EndX=58.0684 EndY=79.9405 EndZ=0
    g4: LineSegment [constr] StartX=-0.019387 StartY=0 StartZ=0 EndX=15.4572 EndY=97.7158 EndZ=0
    g5: LineSegment StartX=14.8002 StartY=93.5675 StartZ=0 EndX=18.7213 EndY=95.0727 EndZ=0
    g6: LineSegment StartX=18.7213 StartY=95.0727 StartZ=0 EndX=19.3783 EndY=99.2209 EndZ=0
    g7: LineSegment StartX=19.3783 StartY=99.2209 StartZ=0 EndX=16.1143 EndY=101.864 EndZ=0
    g8: LineSegment StartX=16.1143 StartY=101.864 StartZ=0 EndX=12.1932 EndY=100.359 EndZ=0
    g9: LineSegment StartX=12.1932 StartY=100.359 StartZ=0 EndX=11.5362 EndY=96.2107 EndZ=0
    g10: LineSegment StartX=11.5362 StartY=96.2107 StartZ=0 EndX=14.8002 EndY=93.5675 EndZ=0
    g11: Circle [constr] CenterX=15.4572 CenterY=97.7158 CenterZ=0 NormalX=0 NormalY=0 NormalZ=1 AngleXU=0 Radius=4.2
    g12: LineSegment StartX=55.5997 StartY=76.5427 StartZ=0 EndX=59.7767 EndY=76.1036 EndZ=0
    g13: LineSegment StartX=59.7767 StartY=76.1036 StartZ=0 EndX=62.2454 EndY=79.5015 EndZ=0
    g14: LineSegment StartX=62.2454 StartY=79.5015 StartZ=0 EndX=60.5371 EndY=83.3384 EndZ=0
    g15: LineSegment StartX=60.5371 StartY=83.3384 StartZ=0 EndX=56.3601 EndY=83.7774 EndZ=0
    g16: LineSegment StartX=56.3601 StartY=83.7774 StartZ=0 EndX=53.8914 EndY=80.3795 EndZ=0
    g17: LineSegment StartX=53.8914 StartY=80.3795 StartZ=0 EndX=55.5997 EndY=76.5427 EndZ=0
    g18: Circle [constr] CenterX=58.0684 CenterY=79.9405 CenterZ=0 NormalX=0 NormalY=0 NormalZ=1 AngleXU=0 Radius=4.2
    g19: LineSegment StartX=76.4623 StartY=55.5532 StartZ=0 EndX=80.2992 EndY=53.8449 EndZ=0
    g20: LineSegment StartX=80.2992 StartY=53.8449 StartZ=0 EndX=83.697 EndY=56.3136 EndZ=0
    g21: LineSegment StartX=83.697 StartY=56.3136 StartZ=0 EndX=83.258 EndY=60.4906 EndZ=0
    g22: LineSegment StartX=83.258 StartY=60.4906 StartZ=0 EndX=79.4211 EndY=62.1988 EndZ=0
    g23: LineSegment StartX=79.4211 StartY=62.1988 StartZ=0 EndX=76.0233 EndY=59.7301 EndZ=0
    g24: LineSegment StartX=76.0233 StartY=59.7301 StartZ=0 EndX=76.4623 EndY=55.5532 EndZ=0
    g25: Circle [constr] CenterX=79.8601 CenterY=58.0219 CenterZ=0 NormalX=0 NormalY=0 NormalZ=1 AngleXU=0 Radius=4.2
    g26: LineSegment StartX=93.227 StartY=14.731 StartZ=0 EndX=95.8702 EndY=11.467 EndZ=0
    g27: LineSegment StartX=95.8702 StartY=11.467 StartZ=0 EndX=100.018 EndY=12.124 EndZ=0
    g28: LineSegment StartX=100.018 StartY=12.124 StartZ=0 EndX=101.524 EndY=16.045 EndZ=0
    g29: LineSegment StartX=101.524 StartY=16.045 StartZ=0 EndX=98.8804 EndY=19.309 EndZ=0
    g30: LineSegment StartX=98.8804 StartY=19.309 StartZ=0 EndX=94.7322 EndY=18.652 EndZ=0
    g31: LineSegment StartX=94.7322 StartY=18.652 StartZ=0 EndX=93.227 EndY=14.731 EndZ=0
    g32: Circle [constr] CenterX=97.3753 CenterY=15.388 CenterZ=0 NormalX=0 NormalY=0 NormalZ=1 AngleXU=0 Radius=4.2
    g33: ArcOfCircle [constr] CenterX=0.20211 CenterY=0.215302 CenterZ=0 NormalX=0 NormalY=0 NormalZ=1 AngleXU=0 Radius=98.75 StartAngle=1.57284 EndAngle=3.14377
    g34: LineSegment [constr] StartX=0 StartY=-0.03476 StartZ=0 EndX=-97.3753 EndY=15.388 EndZ=0
    g35: LineSegment [constr] StartX=0 StartY=0 StartZ=0 EndX=-79.8601 EndY=58.0219 EndZ=0
    g36: LineSegment [constr] StartX=0.011779 StartY=0 StartZ=0 EndX=-58.0684 EndY=79.9405 EndZ=0
    g37: LineSegment [constr] StartX=0.019387 StartY=0 StartZ=0 EndX=-15.4572 EndY=97.7158 EndZ=0
    g38: LineSegment StartX=-14.8002 StartY=93.5675 StartZ=0 EndX=-18.7213 EndY=95.0727 EndZ=0
    g39: LineSegment StartX=-18.7213 StartY=95.0727 StartZ=0 EndX=-19.3783 EndY=99.2209 EndZ=0
    g40: LineSegment StartX=-19.3783 StartY=99.2209 StartZ=0 EndX=-16.1143 EndY=101.864 EndZ=0
    g41: LineSegment StartX=-16.1143 StartY=101.864 StartZ=0 EndX=-12.1932 EndY=100.359 EndZ=0
    g42: LineSegment StartX=-12.1932 StartY=100.359 StartZ=0 EndX=-11.5362 EndY=96.2107 EndZ=0
    g43: LineSegment StartX=-11.5362 StartY=96.2107 StartZ=0 EndX=-14.8002 EndY=93.5675 EndZ=0
    g44: Circle [constr] CenterX=-15.4572 CenterY=97.7158 CenterZ=0 NormalX=0 NormalY=0 NormalZ=1 AngleXU=0 Radius=4.2
    g45: LineSegment StartX=-55.5997 StartY=76.5427 StartZ=0 EndX=-59.7767 EndY=76.1036 EndZ=0
    g46: LineSegment StartX=-59.7767 StartY=76.1036 StartZ=0 EndX=-62.2454 EndY=79.5015 EndZ=0
    g47: LineSegment StartX=-62.2454 StartY=79.5015 StartZ=0 EndX=-60.5371 EndY=83.3384 EndZ=0
    g48: LineSegment StartX=-60.5371 StartY=83.3384 StartZ=0 EndX=-56.3601 EndY=83.7774 EndZ=0
    g49: LineSegment StartX=-56.3601 StartY=83.7774 StartZ=0 EndX=-53.8914 EndY=80.3795 EndZ=0
    g50: LineSegment StartX=-53.8914 StartY=80.3795 StartZ=0 EndX=-55.5997 EndY=76.5427 EndZ=0
    g51: Circle [constr] CenterX=-58.0684 CenterY=79.9405 CenterZ=0 NormalX=0 NormalY=0 NormalZ=1 AngleXU=0 Radius=4.2
    g52: LineSegment StartX=-76.4623 StartY=55.5532 StartZ=0 EndX=-80.2992 EndY=53.8449 EndZ=0
    g53: LineSegment StartX=-80.2992 StartY=53.8449 StartZ=0 EndX=-83.697 EndY=56.3136 EndZ=0
    g54: LineSegment StartX=-83.697 StartY=56.3136 StartZ=0 EndX=-83.258 EndY=60.4906 EndZ=0
    g55: LineSegment StartX=-83.258 StartY=60.4906 StartZ=0 EndX=-79.4211 EndY=62.1988 EndZ=0
    g56: LineSegment StartX=-79.4211 StartY=62.1988 StartZ=0 EndX=-76.0233 EndY=59.7301 EndZ=0
    g57: LineSegment StartX=-76.0233 StartY=59.7301 StartZ=0 EndX=-76.4623 EndY=55.5532 EndZ=0
    g58: Circle [constr] CenterX=-79.8601 CenterY=58.0219 CenterZ=0 NormalX=0 NormalY=0 NormalZ=1 AngleXU=0 Radius=4.2
    g59: LineSegment StartX=-93.227 StartY=14.731 StartZ=0 EndX=-95.8702 EndY=11.467 EndZ=0
    g60: LineSegment StartX=-95.8702 StartY=11.467 StartZ=0 EndX=-100.018 EndY=12.124 EndZ=0
    g61: LineSegment StartX=-100.018 StartY=12.124 StartZ=0 EndX=-101.524 EndY=16.045 EndZ=0
    g62: LineSegment StartX=-101.524 StartY=16.045 StartZ=0 EndX=-98.8804 EndY=19.309 EndZ=0
    g63: LineSegment StartX=-98.8804 StartY=19.309 StartZ=0 EndX=-94.7322 EndY=18.652 EndZ=0
    g64: LineSegment StartX=-94.7322 StartY=18.652 StartZ=0 EndX=-93.227 EndY=14.731 EndZ=0
    g65: Circle [constr] CenterX=-97.3753 CenterY=15.388 CenterZ=0 NormalX=0 NormalY=0 NormalZ=1 AngleXU=0 Radius=4.2
    g66: ArcOfCircle [constr] CenterX=-0.20211 CenterY=-0.215302 CenterZ=0 NormalX=0 NormalY=0 NormalZ=1 AngleXU=0 Radius=98.75 StartAngle=4.71444 EndAngle=6.28537
    g67: LineSegment [constr] StartX=0 StartY=0.03476 StartZ=0 EndX=97.3753 EndY=-15.388 EndZ=0
    g68: LineSegment [constr] StartX=0 StartY=0 StartZ=0 EndX=79.8601 EndY=-58.0219 EndZ=0
    g69: LineSegment [constr] StartX=-0.011779 StartY=0 StartZ=0 EndX=58.0684 EndY=-79.9405 EndZ=0
    g70: LineSegment [constr] StartX=-0.019387 StartY=0 StartZ=0 EndX=15.4572 EndY=-97.7158 EndZ=0
    g71: LineSegment StartX=14.8002 StartY=-93.5675 StartZ=0 EndX=18.7213 EndY=-95.0727 EndZ=0
    g72: LineSegment StartX=18.7213 StartY=-95.0727 StartZ=0 EndX=19.3783 EndY=-99.2209 EndZ=0
    g73: LineSegment StartX=19.3783 StartY=-99.2209 StartZ=0 EndX=16.1143 EndY=-101.864 EndZ=0
    g74: LineSegment StartX=16.1143 StartY=-101.864 StartZ=0 EndX=12.1932 EndY=-100.359 EndZ=0
    g75: LineSegment StartX=12.1932 StartY=-100.359 StartZ=0 EndX=11.5362 EndY=-96.2107 EndZ=0
    g76: LineSegment StartX=11.5362 StartY=-96.2107 StartZ=0 EndX=14.8002 EndY=-93.5675 EndZ=0
    g77: Circle [constr] CenterX=15.4572 CenterY=-97.7158 CenterZ=0 NormalX=0 NormalY=0 NormalZ=1 AngleXU=0 Radius=4.2
    g78: LineSegment StartX=55.5997 StartY=-76.5427 StartZ=0 EndX=59.7767 EndY=-76.1036 EndZ=0
    g79: LineSegment StartX=59.7767 StartY=-76.1036 StartZ=0 EndX=62.2454 EndY=-79.5015 EndZ=0
    g80: LineSegment StartX=62.2454 StartY=-79.5015 StartZ=0 EndX=60.5371 EndY=-83.3384 EndZ=0
    g81: LineSegment StartX=60.5371 StartY=-83.3384 StartZ=0 EndX=56.3601 EndY=-83.7774 EndZ=0
    g82: LineSegment StartX=56.3601 StartY=-83.7774 StartZ=0 EndX=53.8914 EndY=-80.3795 EndZ=0
    g83: LineSegment StartX=53.8914 StartY=-80.3795 StartZ=0 EndX=55.5997 EndY=-76.5427 EndZ=0
    g84: Circle [constr] CenterX=58.0684 CenterY=-79.9405 CenterZ=0 NormalX=0 NormalY=0 NormalZ=1 AngleXU=0 Radius=4.2
    g85: LineSegment StartX=76.4623 StartY=-55.5532 StartZ=0 EndX=80.2992 EndY=-53.8449 EndZ=0
    g86: LineSegment StartX=80.2992 StartY=-53.8449 StartZ=0 EndX=83.697 EndY=-56.3136 EndZ=0
    g87: LineSegment StartX=83.697 StartY=-56.3136 StartZ=0 EndX=83.258 EndY=-60.4906 EndZ=0
    g88: LineSegment StartX=83.258 StartY=-60.4906 StartZ=0 EndX=79.4211 EndY=-62.1988 EndZ=0
    g89: LineSegment StartX=79.4211 StartY=-62.1988 StartZ=0 EndX=76.0233 EndY=-59.7301 EndZ=0
    g90: LineSegment StartX=76.0233 StartY=-59.7301 StartZ=0 EndX=76.4623 EndY=-55.5532 EndZ=0
    g91: Circle [constr] CenterX=79.8601 CenterY=-58.0219 CenterZ=0 NormalX=0 NormalY=0 NormalZ=1 AngleXU=0 Radius=4.2
    g92: LineSegment StartX=93.227 StartY=-14.731 StartZ=0 EndX=95.8702 EndY=-11.467 EndZ=0
    g93: LineSegment StartX=95.8702 StartY=-11.467 StartZ=0 EndX=100.018 EndY=-12.124 EndZ=0
    g94: LineSegment StartX=100.018 StartY=-12.124 StartZ=0 EndX=101.524 EndY=-16.045 EndZ=0
    g95: LineSegment StartX=101.524 StartY=-16.045 StartZ=0 EndX=98.8804 EndY=-19.309 EndZ=0
    g96: LineSegment StartX=98.8804 StartY=-19.309 StartZ=0 EndX=94.7322 EndY=-18.652 EndZ=0
    g97: LineSegment StartX=94.7322 StartY=-18.652 StartZ=0 EndX=93.227 EndY=-14.731 EndZ=0
    g98: Circle [constr] CenterX=97.3753 CenterY=-15.388 CenterZ=0 NormalX=0 NormalY=0 NormalZ=1 AngleXU=0 Radius=4.2
    g99: ArcOfCircle [constr] CenterX=0.20211 CenterY=-0.215302 CenterZ=0 NormalX=0 NormalY=0 NormalZ=1 AngleXU=0 Radius=98.75 StartAngle=3.13941 EndAngle=4.71034
    g100: LineSegment [constr] StartX=0 StartY=0.03476 StartZ=0 EndX=-97.3753 EndY=-15.388 EndZ=0
    g101: LineSegment [constr] StartX=0 StartY=0 StartZ=0 EndX=-79.8601 EndY=-58.0219 EndZ=0
    g102: LineSegment [constr] StartX=0.011779 StartY=0 StartZ=0 EndX=-58.0684 EndY=-79.9405 EndZ=0
    g103: LineSegment [constr] StartX=0.019387 StartY=0 StartZ=0 EndX=-15.4572 EndY=-97.7158 EndZ=0
    g104: LineSegment StartX=-14.8002 StartY=-93.5675 StartZ=0 EndX=-18.7213 EndY=-95.0727 EndZ=0
    g105: LineSegment StartX=-18.7213 StartY=-95.0727 StartZ=0 EndX=-19.3783 EndY=-99.2209 EndZ=0
    g106: LineSegment StartX=-19.3783 StartY=-99.2209 StartZ=0 EndX=-16.1143 EndY=-101.864 EndZ=0
    g107: LineSegment StartX=-16.1143 StartY=-101.864 StartZ=0 EndX=-12.1932 EndY=-100.359 EndZ=0
    g108: LineSegment StartX=-12.1932 StartY=-100.359 StartZ=0 EndX=-11.5362 EndY=-96.2107 EndZ=0
    g109: LineSegment StartX=-11.5362 StartY=-96.2107 StartZ=0 EndX=-14.8002 EndY=-93.5675 EndZ=0
    g110: Circle [constr] CenterX=-15.4572 CenterY=-97.7158 CenterZ=0 NormalX=0 NormalY=0 NormalZ=1 AngleXU=0 Radius=4.2
    g111: LineSegment StartX=-55.5997 StartY=-76.5427 StartZ=0 EndX=-59.7767 EndY=-76.1036 EndZ=0
    g112: LineSegment StartX=-59.7767 StartY=-76.1036 StartZ=0 EndX=-62.2454 EndY=-79.5015 EndZ=0
    g113: LineSegment StartX=-62.2454 StartY=-79.5015 StartZ=0 EndX=-60.5371 EndY=-83.3384 EndZ=0
    g114: LineSegment StartX=-60.5371 StartY=-83.3384 StartZ=0 EndX=-56.3601 EndY=-83.7774 EndZ=0
    g115: LineSegment StartX=-56.3601 StartY=-83.7774 StartZ=0 EndX=-53.8914 EndY=-80.3795 EndZ=0
    g116: LineSegment StartX=-53.8914 StartY=-80.3795 StartZ=0 EndX=-55.5997 EndY=-76.5427 EndZ=0
    g117: Circle [constr] CenterX=-58.0684 CenterY=-79.9405 CenterZ=0 NormalX=0 NormalY=0 NormalZ=1 AngleXU=0 Radius=4.2
    g118: LineSegment StartX=-76.4623 StartY=-55.5532 StartZ=0 EndX=-80.2992 EndY=-53.8449 EndZ=0
    g119: LineSegment StartX=-80.2992 StartY=-53.8449 StartZ=0 EndX=-83.697 EndY=-56.3136 EndZ=0
    g120: LineSegment StartX=-83.697 StartY=-56.3136 StartZ=0 EndX=-83.258 EndY=-60.4906 EndZ=0
    g121: LineSegment StartX=-83.258 StartY=-60.4906 StartZ=0 EndX=-79.4211 EndY=-62.1988 EndZ=0
    g122: LineSegment StartX=-79.4211 StartY=-62.1988 StartZ=0 EndX=-76.0233 EndY=-59.7301 EndZ=0
    g123: LineSegment StartX=-76.0233 StartY=-59.7301 StartZ=0 EndX=-76.4623 EndY=-55.5532 EndZ=0
    g124: Circle [constr] CenterX=-79.8601 CenterY=-58.0219 CenterZ=0 NormalX=0 NormalY=0 NormalZ=1 AngleXU=0 Radius=4.2
    g125: LineSegment StartX=-93.227 StartY=-14.731 StartZ=0 EndX=-95.8702 EndY=-11.467 EndZ=0
    g126: LineSegment StartX=-95.8702 StartY=-11.467 StartZ=0 EndX=-100.018 EndY=-12.124 EndZ=0
    g127: LineSegment StartX=-100.018 StartY=-12.124 StartZ=0 EndX=-101.524 EndY=-16.045 EndZ=0
    g128: LineSegment StartX=-101.524 StartY=-16.045 StartZ=0 EndX=-98.8804 EndY=-19.309 EndZ=0
    g129: LineSegment StartX=-98.8804 StartY=-19.309 StartZ=0 EndX=-94.7322 EndY=-18.652 EndZ=0
    g130: LineSegment StartX=-94.7322 StartY=-18.652 StartZ=0 EndX=-93.227 EndY=-14.731 EndZ=0
    g131: Circle [constr] CenterX=-97.3753 CenterY=-15.388 CenterZ=0 NormalX=0 NormalY=0 NormalZ=1 AngleXU=0 Radius=4.2
  constraints (282):
    c: Radius(g0) = 98.75
    c: PointOnObject(g0,g-1)
    c: PointOnObject(g0,g-2)
    c: Angle(g-1,g1) = 0.15708
    c: PointOnObject(g1,g0)
    c: Angle(g-1,g2) = 0.628319
    c: PointOnObject(g2,g0)
    c: Angle(g-1,g3) = 0.942478
    c: PointOnObject(g3,g0)
    c: Angle(g-1,g4) = 1.41372
    c: PointOnObject(g4,g0)
    c: Coincident(g5,g6)
    c: Coincident(g6,g7)
    c: Coincident(g7,g8)
    c: Coincident(g8,g9)
    c: Coincident(g9,g10)
    c: Coincident(g10,g5)
    c: Equal(g5, g6-g10) x5
    c: PointOnObject(g5,g11)
    c: PointOnObject(g6,g11)
    c: PointOnObject(g7,g11)
    c: PointOnObject(g8,g11)
    c: PointOnObject(g9,g11)
    c: PointOnObject(g10,g11)
    c: Radius(g11) = 4.2
    c: Coincident(g11,g4)
    c: PointOnObject(g10,g4)
    c: Coincident(g12,g13)
    c: Coincident(g13,g14)
    c: Coincident(g14,g15)
    c: Coincident(g15,g16)
    c: Coincident(g16,g17)
    c: Coincident(g17,g12)
    c: Equal(g12, g13-g17) x5
    c: PointOnObject(g12,g18)
    c: PointOnObject(g13,g18)
    c: PointOnObject(g14,g18)
    c: PointOnObject(g15,g18)
    c: PointOnObject(g16,g18)
    c: PointOnObject(g17,g18)
    c: Radius(g18) = 4.2
    c: Coincident(g18,g3)
    c: PointOnObject(g17,g3)
    c: Coincident(g19,g20)
    c: Coincident(g20,g21)
    c: Coincident(g21,g22)
    c: Coincident(g22,g23)
    c: Coincident(g23,g24)
    c: Coincident(g24,g19)
    c: Equal(g19, g20-g24) x5
    c: PointOnObject(g19,g25)
    c: PointOnObject(g20,g25)
    c: PointOnObject(g21,g25)
    c: PointOnObject(g22,g25)
    c: PointOnObject(g23,g25)
    c: PointOnObject(g24,g25)
    c: Radius(g25) = 4.2
    c: Coincident(g25,g2)
    c: PointOnObject(g24,g2)
    c: Coincident(g26,g27)
    c: Coincident(g27,g28)
    c: Coincident(g28,g29)
    c: Coincident(g29,g30)
    c: Coincident(g30,g31)
    c: Coincident(g31,g26)
    c: Equal(g26, g27-g31) x5
    c: PointOnObject(g26,g32)
    c: PointOnObject(g27,g32)
    c: PointOnObject(g28,g32)
    c: PointOnObject(g29,g32)
    c: PointOnObject(g30,g32)
    c: PointOnObject(g31,g32)
    c: Radius(g32) = 4.2
    c: Coincident(g32,g1)
    c: PointOnObject(g31,g1)
    c: Radius(g33) = 98.75
    c: PointOnObject(g34,g33)
    c: PointOnObject(g35,g33)
    c: PointOnObject(g36,g33)
    c: PointOnObject(g37,g33)
    c: Coincident(g38,g39)
    c: Coincident(g39,g40)
    c: Coincident(g40,g41)
    c: Coincident(g41,g42)
    c: Coincident(g42,g43)
    c: Coincident(g43,g38)
    c: Equal(g38, g39-g43) x5
    c: PointOnObject(g38,g44)
    c: PointOnObject(g39,g44)
    c: PointOnObject(g40,g44)
    c: PointOnObject(g41,g44)
    c: PointOnObject(g42,g44)
    c: PointOnObject(g43,g44)
    c: Radius(g44) = 4.2
    c: Coincident(g44,g37)
    c: PointOnObject(g43,g37)
    c: Coincident(g45,g46)
    c: Coincident(g46,g47)
    c: Coincident(g47,g48)
    c: Coincident(g48,g49)
    c: Coincident(g49,g50)
    c: Coincident(g50,g45)
    c: Equal(g45, g46-g50) x5
    c: PointOnObject(g45,g51)
    c: PointOnObject(g46,g51)
    c: PointOnObject(g47,g51)
    c: PointOnObject(g48,g51)
    c: PointOnObject(g49,g51)
    c: PointOnObject(g50,g51)
    c: Radius(g51) = 4.2
    c: Coincident(g51,g36)
    c: PointOnObject(g50,g36)
    c: Coincident(g52,g53)
    c: Coincident(g53,g54)
    c: Coincident(g54,g55)
    c: Coincident(g55,g56)
    c: Coincident(g56,g57)
    c: Coincident(g57,g52)
    c: Equal(g52, g53-g57) x5
    c: PointOnObject(g52,g58)
    c: PointOnObject(g53,g58)
    c: PointOnObject(g54,g58)
    c: PointOnObject(g55,g58)
    c: PointOnObject(g56,g58)
    c: PointOnObject(g57,g58)
    c: Radius(g58) = 4.2
    c: Coincident(g58,g35)
    c: PointOnObject(g57,g35)
    c: Coincident(g59,g60)
    c: Coincident(g60,g61)
    c: Coincident(g61,g62)
    c: Coincident(g62,g63)
    c: Coincident(g63,g64)
    c: Coincident(g64,g59)
    c: Equal(g59, g60-g64) x5
    c: PointOnObject(g59,g65)
    c: PointOnObject(g60,g65)
    c: PointOnObject(g61,g65)
    c: PointOnObject(g62,g65)
    c: PointOnObject(g63,g65)
    c: PointOnObject(g64,g65)
    c: Radius(g65) = 4.2
    c: Coincident(g65,g34)
    c: PointOnObject(g64,g34)
    c: Radius(g66) = 98.75
    c: PointOnObject(g67,g66)
    c: PointOnObject(g68,g66)
    c: PointOnObject(g69,g66)
    c: PointOnObject(g70,g66)
    c: Coincident(g71,g72)
    c: Coincident(g72,g73)
    c: Coincident(g73,g74)
    c: Coincident(g74,g75)
    c: Coincident(g75,g76)
    c: Coincident(g76,g71)
    c: Equal(g71, g72-g76) x5
    c: PointOnObject(g71,g77)
    c: PointOnObject(g72,g77)
    c: PointOnObject(g73,g77)
    c: PointOnObject(g74,g77)
    c: PointOnObject(g75,g77)
    c: PointOnObject(g76,g77)
    c: Radius(g77) = 4.2
    c: Coincident(g77,g70)
    c: PointOnObject(g76,g70)
    c: Coincident(g78,g79)
    c: Coincident(g79,g80)
    c: Coincident(g80,g81)
    c: Coincident(g81,g82)
    c: Coincident(g82,g83)
    c: Coincident(g83,g78)
    c: Equal(g78, g79-g83) x5
    c: PointOnObject(g78,g84)
    c: PointOnObject(g79,g84)
    c: PointOnObject(g80,g84)
    c: PointOnObject(g81,g84)
    c: PointOnObject(g82,g84)
    c: PointOnObject(g83,g84)
    c: Radius(g84) = 4.2
    c: Coincident(g84,g69)
    c: PointOnObject(g83,g69)
    c: Coincident(g85,g86)
    c: Coincident(g86,g87)
    c: Coincident(g87,g88)
    c: Coincident(g88,g89)
    c: Coincident(g89,g90)
    c: Coincident(g90,g85)
    c: Equal(g85, g86-g90) x5
    c: PointOnObject(g85,g91)
    c: PointOnObject(g86,g91)
    c: PointOnObject(g87,g91)
    c: PointOnObject(g88,g91)
    c: PointOnObject(g89,g91)
    c: PointOnObject(g90,g91)
    c: Radius(g91) = 4.2
    c: Coincident(g91,g68)
    c: PointOnObject(g90,g68)
    c: Coincident(g92,g93)
    c: Coincident(g93,g94)
    c: Coincident(g94,g95)
    c: Coincident(g95,g96)
    c: Coincident(g96,g97)
    c: Coincident(g97,g92)
    c: Equal(g92, g93-g97) x5
    c: PointOnObject(g92,g98)
    c: PointOnObject(g93,g98)
    c: PointOnObject(g94,g98)
    c: PointOnObject(g95,g98)
    c: PointOnObject(g96,g98)
    c: PointOnObject(g97,g98)
    c: Radius(g98) = 4.2
    c: Coincident(g98,g67)
    c: PointOnObject(g97,g67)
    c: Radius(g99) = 98.75
    c: PointOnObject(g100,g99)
    c: PointOnObject(g101,g99)
    c: PointOnObject(g102,g99)
    c: PointOnObject(g103,g99)
    c: Coincident(g104,g105)
    c: Coincident(g105,g106)
    c: Coincident(g106,g107)
    c: Coincident(g107,g108)
    c: Coincident(g108,g109)
    c: Coincident(g109,g104)
    c: Equal(g104, g105-g109) x5
    c: PointOnObject(g104,g110)
    c: PointOnObject(g105,g110)
    c: PointOnObject(g106,g110)
    c: PointOnObject(g107,g110)
    c: PointOnObject(g108,g110)
    c: PointOnObject(g109,g110)
    c: Radius(g110) = 4.2
    c: Coincident(g110,g103)
    c: PointOnObject(g109,g103)
    c: Coincident(g111,g112)
    c: Coincident(g112,g113)
    c: Coincident(g113,g114)
    c: Coincident(g114,g115)
    c: Coincident(g115,g116)
    c: Coincident(g116,g111)
    c: Equal(g111, g112-g116) x5
    c: PointOnObject(g111,g117)
    c: PointOnObject(g112,g117)
    c: PointOnObject(g113,g117)
    c: PointOnObject(g114,g117)
    c: PointOnObject(g115,g117)
    c: PointOnObject(g116,g117)
    c: Radius(g117) = 4.2
    c: Coincident(g117,g102)
    c: PointOnObject(g116,g102)
    c: Coincident(g118,g119)
    c: Coincident(g119,g120)
    c: Coincident(g120,g121)
    c: Coincident(g121,g122)
    c: Coincident(g122,g123)
    c: Coincident(g123,g118)
    c: Equal(g118, g119-g123) x5
    c: PointOnObject(g118,g124)
    c: PointOnObject(g119,g124)
    c: PointOnObject(g120,g124)
    c: PointOnObject(g121,g124)
    c: PointOnObject(g122,g124)
    c: PointOnObject(g123,g124)
    c: Radius(g124) = 4.2
    c: Coincident(g124,g101)
    c: PointOnObject(g123,g101)
    c: Coincident(g125,g126)
    c: Coincident(g126,g127)
    c: Coincident(g127,g128)
    c: Coincident(g128,g129)
    c: Coincident(g129,g130)
    c: Coincident(g130,g125)
    c: Equal(g125, g126-g130) x5
    c: PointOnObject(g125,g131)
    c: PointOnObject(g126,g131)
    c: PointOnObject(g127,g131)
    c: PointOnObject(g128,g131)
    c: PointOnObject(g129,g131)
    c: PointOnObject(g130,g131)
    c: Radius(g131) = 4.2
    c: Coincident(g131,g100)
    c: PointOnObject(g130,g100)
FEATURE [PartDesign::Pocket] Pocket013
  BaseFeature = -> Pad008
  Direction = (0,0,1)
  Length = 3.7
  Length2 = 5
  Profile = -> Sketch036
  ReferenceAxis = -> Sketch036 [N_Axis]
  Refine = true
  Suppressed = false
  Type = 0
FEATURE [PartDesign::Body] Body003  label="CaseB"
  AllowCompound = false
  Group = -> [Sketch006,Pad002,Sketch007,Pocket001,Sketch008,Pocket002,Sketch009,Pad008,Sketch036,Pocket013]
  Origin = -> Origin003
  Placement = pos=(0,0,8.7) rot=(0,0,1;0rad)
  Tip = -> Pocket013
FEATURE [PartDesign::Plane] DatumPlane002
  AttachmentSupport = -> [Pad007]
  Length = 179.756
  MapMode = 5
  Placement = pos=(-6.63e-14,4.14e-14,0) rot=(0.787007,0.436245,0.436245;1.80806rad)
  ResizeMode = 0
  Width = 67.9872
FEATURE [PartDesign::Line] DatumLine
  AttacherType = Attacher::AttachEngineLine
  AttachmentSupport = -> [Pad007]
  Length = 20
  MapMode = 29
  Placement = pos=(-7.82e-14,2.84e-14,0) rot=(0.198716,0.693005,0.693005;2.74927rad)
  ResizeMode = 0
FEATURE [PartDesign::Line] DatumLine001
  AttacherType = Attacher::AttachEngineLine
  AttachmentSupport = -> [Pad007]
  Length = 20
  MapMode = 29
  Placement = pos=(60.9407,97.5255,0) rot=(0,0,1;0rad)
  ResizeMode = 0
FEATURE [PartDesign::Line] DatumLine002
  AttacherType = Attacher::AttachEngineLine
  AttachmentSupport = -> [Pad007]
  Length = 20
  MapMode = 29
  Placement = pos=(44.2483,70.812,0) rot=(0,0,1;0rad)
  ResizeMode = 0
FEATURE [Sketcher::SketchObject] Sketch040
  ArcFitTolerance = 1e-06
  AttachmentSupport = -> [DatumPlane002]
  FullyConstrained = true
  MakeInternals = false
  MapMode = 5
  Placement = pos=(-6.63e-14,4.14e-14,0) rot=(0.787007,0.436245,0.436245;1.80806rad)
FEATURE [Sketcher::SketchObject] Sketch041
  ArcFitTolerance = 1e-06
  AttachmentSupport = -> [DatumPlane002]
  FullyConstrained = true
  MakeInternals = false
  MapMode = 5
  Placement = pos=(-6.63e-14,4.14e-14,0) rot=(0.787007,0.436245,0.436245;1.80806rad)
  sketch-geometry (5):
    g0: LineSegment StartX=110 StartY=0 StartZ=0 EndX=110 EndY=2 EndZ=0
    g1: LineSegment StartX=110 StartY=2 StartZ=0 EndX=90.0001 EndY=2 EndZ=0
    g2: LineSegment StartX=90.0001 StartY=2 StartZ=0 EndX=90.0001 EndY=0 EndZ=0
    g3: LineSegment StartX=90.0001 StartY=0 StartZ=0 EndX=110 EndY=0 EndZ=0
    g4: LineSegment [constr] StartX=115 StartY=0 StartZ=0 EndX=115 EndY=2 EndZ=0
  constraints (15):
    c: Coincident(g0,g1)
    c: Coincident(g1,g2)
    c: Coincident(g2,g3)
    c: Coincident(g3,g0)
    c: Vertical(g0)
    c: Vertical(g2)
    c: Horizontal(g1)
    c: Horizontal(g3)
    c: PointOnObject(g0,g-1)
    c: Distance(g0,g2) = 20
    c: Distance(g4) = 2
    c: PointOnObject(g4,g-1)
    c: Block(g4)
    c: Distance(g0,g4) = 5
    c: Distance(g2,g2) = 2
FEATURE [PartDesign::Pad] Pad018
  BaseFeature = -> Pad007
  Direction = (0.848048,-0.529919,2e-16)
  Length = 2
  Length2 = 10
  Profile = -> Sketch041
  ReferenceAxis = -> Sketch041 [N_Axis]
  Refine = true
  Suppressed = false
  Type = 0
FEATURE [PartDesign::Plane] DatumPlane003
  AttachmentSupport = -> [Pad018]
  Length = 170.358
  MapMode = 5
  Placement = pos=(9.69e-14,-2.24e-14,0) rot=(-0.490233,0.616308,0.616308;4.0532rad)
  ResizeMode = 0
  Width = 67.4856
FEATURE [PartDesign::Plane] DatumPlane004
  AttachmentSupport = -> [Pocket012]
  Length = 275.873
  MapMode = 5
  Placement = pos=(0,0,10) rot=(1,0,0;3.14159rad)
  ResizeMode = 0
  Width = 275.863
FEATURE [Sketcher::SketchObject] Sketch043
  ArcFitTolerance = 1e-06
  AttachmentSupport = -> [DatumPlane004]
  FullyConstrained = false
  MakeInternals = false
  MapMode = 5
  Placement = pos=(0,0,10) rot=(1,0,0;3.14159rad)
  sketch-geometry (72):
    g0: LineSegment StartX=85.8924 StartY=16.6958 StartZ=0 EndX=108.961 EndY=21.1798 EndZ=0
    g1: LineSegment StartX=72.5408 StartY=48.9294 StartZ=0 EndX=92.0232 EndY=62.0704 EndZ=0
    g2: LineSegment [constr] StartX=0 StartY=0 StartZ=0 EndX=81.3173 EndY=81.3173 EndZ=0
    g3: LineSegment StartX=74.0012 StartY=46.6913 StartZ=0 EndX=93.8758 EndY=59.2312 EndZ=0
    g4: ArcOfCircle CenterX=0 CenterY=0 CenterZ=0 NormalX=0 NormalY=0 NormalZ=1 AngleXU=0 Radius=87.5 StartAngle=0.191986 EndAngle=0.222529
    g5: ArcOfCircle CenterX=0 CenterY=0 CenterZ=0 NormalX=0 NormalY=0 NormalZ=1 AngleXU=0 Radius=111 StartAngle=0.191986 EndAngle=0.222529
    g6: LineSegment StartX=85.3425 StartY=19.311 StartZ=0 EndX=108.263 EndY=24.4974 EndZ=0
    g7: ArcOfCircle CenterX=0 CenterY=0 CenterZ=0 NormalX=0 NormalY=0 NormalZ=1 AngleXU=0 Radius=87.5 StartAngle=0.562869 EndAngle=0.593412
    g8: ArcOfCircle CenterX=0 CenterY=0 CenterZ=0 NormalX=0 NormalY=0 NormalZ=1 AngleXU=0 Radius=111 StartAngle=0.562869 EndAngle=0.593412
    g9: LineSegment StartX=16.6958 StartY=85.8924 StartZ=0 EndX=21.1798 EndY=108.961 EndZ=0
    g10: LineSegment StartX=48.9294 StartY=72.5408 StartZ=0 EndX=62.0704 EndY=92.0232 EndZ=0
    g11: LineSegment [constr] StartX=0 StartY=0 StartZ=0 EndX=81.3173 EndY=81.3173 EndZ=0
    g12: LineSegment StartX=46.6913 StartY=74.0012 StartZ=0 EndX=59.2312 EndY=93.8758 EndZ=0
    g13: ArcOfCircle CenterX=0 CenterY=0 CenterZ=0 NormalX=0 NormalY=0 NormalZ=1 AngleXU=0 Radius=87.5 StartAngle=1.34827 EndAngle=1.37881
    g14: ArcOfCircle CenterX=0 CenterY=0 CenterZ=0 NormalX=0 NormalY=0 NormalZ=1 AngleXU=0 Radius=111 StartAngle=1.34827 EndAngle=1.37881
    g15: LineSegment StartX=19.3111 StartY=85.3424 StartZ=0 EndX=24.4975 EndY=108.263 EndZ=0
    g16: ArcOfCircle CenterX=0 CenterY=0 CenterZ=0 NormalX=0 NormalY=0 NormalZ=1 AngleXU=0 Radius=87.5 StartAngle=0.977384 EndAngle=1.00793
    g17: ArcOfCircle CenterX=0 CenterY=0 CenterZ=0 NormalX=0 NormalY=0 NormalZ=1 AngleXU=0 Radius=111 StartAngle=0.977384 EndAngle=1.00793
    g18: LineSegment StartX=-85.8924 StartY=16.6958 StartZ=0 EndX=-108.961 EndY=21.1798 EndZ=0
    g19: LineSegment StartX=-72.5408 StartY=48.9294 StartZ=0 EndX=-92.0232 EndY=62.0704 EndZ=0
    g20: LineSegment [constr] StartX=0 StartY=0 StartZ=0 EndX=-81.3173 EndY=81.3173 EndZ=0
    g21: LineSegment StartX=-74.0012 StartY=46.6913 StartZ=0 EndX=-93.8758 EndY=59.2312 EndZ=0
    g22: ArcOfCircle CenterX=0 CenterY=0 CenterZ=0 NormalX=0 NormalY=0 NormalZ=1 AngleXU=0 Radius=87.5 StartAngle=2.91906 EndAngle=2.94961
    g23: ArcOfCircle CenterX=0 CenterY=0 CenterZ=0 NormalX=0 NormalY=0 NormalZ=1 AngleXU=0 Radius=111 StartAngle=2.91906 EndAngle=2.94961
    g24: LineSegment StartX=-85.3425 StartY=19.311 StartZ=0 EndX=-108.263 EndY=24.4974 EndZ=0
    g25: ArcOfCircle CenterX=0 CenterY=0 CenterZ=0 NormalX=0 NormalY=0 NormalZ=1 AngleXU=0 Radius=87.5 StartAngle=2.54818 EndAngle=2.57872
    g26: ArcOfCircle CenterX=0 CenterY=0 CenterZ=0 NormalX=0 NormalY=0 NormalZ=1 AngleXU=0 Radius=111 StartAngle=2.54818 EndAngle=2.57872
    g27: LineSegment StartX=-16.6958 StartY=85.8924 StartZ=0 EndX=-21.1798 EndY=108.961 EndZ=0
    g28: LineSegment StartX=-48.9294 StartY=72.5408 StartZ=0 EndX=-62.0704 EndY=92.0232 EndZ=0
    g29: LineSegment [constr] StartX=0 StartY=0 StartZ=0 EndX=-81.3173 EndY=81.3173 EndZ=0
    g30: LineSegment StartX=-46.6913 StartY=74.0012 StartZ=0 EndX=-59.2312 EndY=93.8758 EndZ=0
    g31: ArcOfCircle CenterX=0 CenterY=0 CenterZ=0 NormalX=0 NormalY=0 NormalZ=1 AngleXU=0 Radius=87.5 StartAngle=1.76278 EndAngle=1.79333
    g32: ArcOfCircle CenterX=0 CenterY=0 CenterZ=0 NormalX=0 NormalY=0 NormalZ=1 AngleXU=0 Radius=111 StartAngle=1.76278 EndAngle=1.79333
    g33: LineSegment StartX=-19.3111 StartY=85.3424 StartZ=0 EndX=-24.4975 EndY=108.263 EndZ=0
    g34: ArcOfCircle CenterX=0 CenterY=0 CenterZ=0 NormalX=0 NormalY=0 NormalZ=1 AngleXU=0 Radius=87.5 StartAngle=2.13367 EndAngle=2.16421
    g35: ArcOfCircle CenterX=0 CenterY=0 CenterZ=0 NormalX=0 NormalY=0 NormalZ=1 AngleXU=0 Radius=111 StartAngle=2.13367 EndAngle=2.16421
    g36: LineSegment StartX=85.8924 StartY=-16.6958 StartZ=0 EndX=108.961 EndY=-21.1798 EndZ=0
    g37: LineSegment StartX=72.5408 StartY=-48.9294 StartZ=0 EndX=92.0232 EndY=-62.0704 EndZ=0
    g38: LineSegment [constr] StartX=0 StartY=0 StartZ=0 EndX=81.3173 EndY=-81.3173 EndZ=0
    g39: LineSegment StartX=74.0012 StartY=-46.6913 StartZ=0 EndX=93.8758 EndY=-59.2312 EndZ=0
    g40: ArcOfCircle CenterX=0 CenterY=0 CenterZ=0 NormalX=0 NormalY=0 NormalZ=1 AngleXU=0 Radius=87.5 StartAngle=6.06066 EndAngle=6.0912
    g41: ArcOfCircle CenterX=0 CenterY=0 CenterZ=0 NormalX=0 NormalY=0 NormalZ=1 AngleXU=0 Radius=111 StartAngle=6.06066 EndAngle=6.0912
    g42: LineSegment StartX=85.3425 StartY=-19.311 StartZ=0 EndX=108.263 EndY=-24.4974 EndZ=0
    g43: ArcOfCircle CenterX=0 CenterY=0 CenterZ=0 NormalX=0 NormalY=0 NormalZ=1 AngleXU=0 Radius=87.5 StartAngle=5.68977 EndAngle=5.72032
    g44: ArcOfCircle CenterX=0 CenterY=0 CenterZ=0 NormalX=0 NormalY=0 NormalZ=1 AngleXU=0 Radius=111 StartAngle=5.68977 EndAngle=5.72032
    g45: LineSegment StartX=16.6958 StartY=-85.8924 StartZ=0 EndX=21.1798 EndY=-108.961 EndZ=0
    g46: LineSegment StartX=48.9294 StartY=-72.5408 StartZ=0 EndX=62.0704 EndY=-92.0232 EndZ=0
    g47: LineSegment [constr] StartX=0 StartY=0 StartZ=0 EndX=81.3173 EndY=-81.3173 EndZ=0
    g48: LineSegment StartX=46.6913 StartY=-74.0012 StartZ=0 EndX=59.2312 EndY=-93.8758 EndZ=0
    g49: ArcOfCircle CenterX=0 CenterY=0 CenterZ=0 NormalX=0 NormalY=0 NormalZ=1 AngleXU=0 Radius=87.5 StartAngle=4.90438 EndAngle=4.93492
    g50: ArcOfCircle CenterX=0 CenterY=0 CenterZ=0 NormalX=0 NormalY=0 NormalZ=1 AngleXU=0 Radius=111 StartAngle=4.90438 EndAngle=4.93492
    g51: LineSegment StartX=19.3111 StartY=-85.3424 StartZ=0 EndX=24.4975 EndY=-108.263 EndZ=0
    g52: ArcOfCircle CenterX=0 CenterY=0 CenterZ=0 NormalX=0 NormalY=0 NormalZ=1 AngleXU=0 Radius=87.5 StartAngle=5.27526 EndAngle=5.3058
    g53: ArcOfCircle CenterX=0 CenterY=0 CenterZ=0 NormalX=0 NormalY=0 NormalZ=1 AngleXU=0 Radius=111 StartAngle=5.27526 EndAngle=5.3058
    g54: LineSegment StartX=-85.8924 StartY=-16.6958 StartZ=0 EndX=-108.961 EndY=-21.1798 EndZ=0
    g55: LineSegment StartX=-72.5408 StartY=-48.9294 StartZ=0 EndX=-92.0232 EndY=-62.0704 EndZ=0
    g56: LineSegment [constr] StartX=0 StartY=0 StartZ=0 EndX=-81.3173 EndY=-81.3173 EndZ=0
    g57: LineSegment StartX=-74.0012 StartY=-46.6913 StartZ=0 EndX=-93.8758 EndY=-59.2312 EndZ=0
    g58: ArcOfCircle CenterX=0 CenterY=0 CenterZ=0 NormalX=0 NormalY=0 NormalZ=1 AngleXU=0 Radius=87.5 StartAngle=3.33358 EndAngle=3.36412
    g59: ArcOfCircle CenterX=0 CenterY=0 CenterZ=0 NormalX=0 NormalY=0 NormalZ=1 AngleXU=0 Radius=111 StartAngle=3.33358 EndAngle=3.36412
    g60: LineSegment StartX=-85.3425 StartY=-19.311 StartZ=0 EndX=-108.263 EndY=-24.4974 EndZ=0
    g61: ArcOfCircle CenterX=0 CenterY=0 CenterZ=0 NormalX=0 NormalY=0 NormalZ=1 AngleXU=0 Radius=87.5 StartAngle=3.70446 EndAngle=3.735
    g62: ArcOfCircle CenterX=0 CenterY=0 CenterZ=0 NormalX=0 NormalY=0 NormalZ=1 AngleXU=0 Radius=111 StartAngle=3.70446 EndAngle=3.735
    g63: LineSegment StartX=-16.6958 StartY=-85.8924 StartZ=0 EndX=-21.1798 EndY=-108.961 EndZ=0
    g64: LineSegment StartX=-48.9294 StartY=-72.5408 StartZ=0 EndX=-62.0704 EndY=-92.0232 EndZ=0
    g65: LineSegment [constr] StartX=0 StartY=0 StartZ=0 EndX=-81.3173 EndY=-81.3173 EndZ=0
    g66: LineSegment StartX=-46.6913 StartY=-74.0012 StartZ=0 EndX=-59.2312 EndY=-93.8758 EndZ=0
    g67: ArcOfCircle CenterX=0 CenterY=0 CenterZ=0 NormalX=0 NormalY=0 NormalZ=1 AngleXU=0 Radius=87.5 StartAngle=4.48986 EndAngle=4.5204
    g68: ArcOfCircle CenterX=0 CenterY=0 CenterZ=0 NormalX=0 NormalY=0 NormalZ=1 AngleXU=0 Radius=111 StartAngle=4.48986 EndAngle=4.5204
    g69: LineSegment StartX=-19.3111 StartY=-85.3424 StartZ=0 EndX=-24.4975 EndY=-108.263 EndZ=0
    g70: ArcOfCircle CenterX=0 CenterY=0 CenterZ=0 NormalX=0 NormalY=0 NormalZ=1 AngleXU=0 Radius=87.5 StartAngle=4.11898 EndAngle=4.14952
    g71: ArcOfCircle CenterX=0 CenterY=0 CenterZ=0 NormalX=0 NormalY=0 NormalZ=1 AngleXU=0 Radius=111 StartAngle=4.11898 EndAngle=4.14952
  constraints (150):
    c: Angle(g-1,g0) = 0.191986
    c: Angle(g-1,g1) = 0.593412
    c: Distance(g2) = 115
    c: Angle(g-1,g2) = 0.785398
    c: Coincident(g2,g-1)
    c: Angle(g3,g1) = 0.0305433
    c: Diameter(g4) = 175
    c: Coincident(g4,g-1)
    c: Diameter(g5) = 222
    c: Coincident(g5,g-1)
    c: Angle(g0,g6) = 0.0305433
    c: Equal(g4,g7)
    c: Coincident(g4,g7)
    c: Coincident(g3,g7)
    c: Coincident(g6,g4)
    c: Coincident(g1,g8)
    c: PointOnObject(g3,g8)
    c: Coincident(g0,g5)
    c: Equal(g5,g8)
    c: Coincident(g5,g6)
    c: PointOnObject(g8,g3)
    c: Coincident(g5,g8)
    c: Coincident(g1,g7)
    c: Coincident(g0,g4)
    c: Distance(g11) = 115
    c: Angle(g12,g10) = -0.0305433
    c: Diameter(g13) = 175
    c: Diameter(g14) = 222
    c: Angle(g9,g15) = -0.0305433
    c: Equal(g13,g16)
    c: Coincident(g13,g16)
    c: Coincident(g12,g16)
    c: Coincident(g15,g13)
    c: Coincident(g10,g17)
    c: PointOnObject(g12,g17)
    c: Coincident(g9,g14)
    c: Equal(g14,g17)
    c: Coincident(g14,g15)
    c: PointOnObject(g17,g12)
    c: Coincident(g14,g17)
    c: Coincident(g10,g16)
    c: Coincident(g9,g13)
    c: Distance(g20) = 115
    c: Angle(g21,g19) = -0.0305433
    c: Diameter(g22) = 175
    c: Diameter(g23) = 222
    c: Angle(g18,g24) = -0.0305433
    c: Equal(g22,g25)
    c: Coincident(g22,g25)
    c: Coincident(g21,g25)
    c: Coincident(g24,g22)
    c: Coincident(g19,g26)
    c: PointOnObject(g21,g26)
    c: Coincident(g18,g23)
    c: Equal(g23,g26)
    c: Coincident(g23,g24)
    c: PointOnObject(g26,g21)
    c: Coincident(g23,g26)
    c: Coincident(g19,g25)
    c: Coincident(g18,g22)
    c: Distance(g29) = 115
    c: Angle(g30,g28) = 0.0305433
    c: Diameter(g31) = 175
    c: Diameter(g32) = 222
    c: Angle(g27,g33) = 0.0305433
    c: Equal(g31,g34)
    c: Coincident(g31,g34)
    c: Coincident(g30,g34)
    c: Coincident(g33,g31)
    c: Coincident(g28,g35)
    c: PointOnObject(g30,g35)
    c: Coincident(g27,g32)
    c: Equal(g32,g35)
    c: Coincident(g32,g33)
    c: PointOnObject(g35,g30)
    c: Coincident(g32,g35)
    c: Coincident(g28,g34)
    c: Coincident(g27,g31)
    c: Distance(g38) = 115
    c: Angle(g39,g37) = -0.0305433
    c: Diameter(g40) = 175
    c: Diameter(g41) = 222
    c: Angle(g36,g42) = -0.0305433
    c: Equal(g40,g43)
    c: Coincident(g40,g43)
    c: Coincident(g39,g43)
    c: Coincident(g42,g40)
    c: Coincident(g37,g44)
    c: PointOnObject(g39,g44)
    c: Coincident(g36,g41)
    c: Equal(g41,g44)
    c: Coincident(g41,g42)
    c: PointOnObject(g44,g39)
    c: Coincident(g41,g44)
    c: Coincident(g37,g43)
    c: Coincident(g36,g40)
    c: Distance(g47) = 115
    c: Angle(g48,g46) = 0.0305433
    c: Diameter(g49) = 175
    c: Diameter(g50) = 222
    c: Angle(g45,g51) = 0.0305433
    c: Equal(g49,g52)
    c: Coincident(g49,g52)
    c: Coincident(g48,g52)
    c: Coincident(g51,g49)
    c: Coincident(g46,g53)
    c: PointOnObject(g48,g53)
    c: Coincident(g45,g50)
    c: Equal(g50,g53)
    c: Coincident(g50,g51)
    c: PointOnObject(g53,g48)
    c: Coincident(g50,g53)
    c: Coincident(g46,g52)
    c: Coincident(g45,g49)
    c: Distance(g56) = 115
    c: Angle(g57,g55) = 0.0305433
    c: Diameter(g58) = 175
    c: Diameter(g59) = 222
    c: Angle(g54,g60) = 0.0305433
    c: Equal(g58,g61)
    c: Coincident(g58,g61)
    c: Coincident(g57,g61)
    c: Coincident(g60,g58)
    c: Coincident(g55,g62)
    c: PointOnObject(g57,g62)
    c: Coincident(g54,g59)
    c: Equal(g59,g62)
    c: Coincident(g59,g60)
    c: PointOnObject(g62,g57)
    c: Coincident(g59,g62)
    c: Coincident(g55,g61)
    c: Coincident(g54,g58)
    c: Distance(g65) = 115
    c: Angle(g66,g64) = -0.0305433
    c: Diameter(g67) = 175
    c: Diameter(g68) = 222
    c: Angle(g63,g69) = -0.0305433
    c: Equal(g67,g70)
    c: Coincident(g67,g70)
    c: Coincident(g66,g70)
    c: Coincident(g69,g67)
    c: Coincident(g64,g71)
    c: PointOnObject(g66,g71)
    c: Coincident(g63,g68)
    c: Equal(g68,g71)
    c: Coincident(g68,g69)
    c: PointOnObject(g71,g66)
    c: Coincident(g68,g71)
    c: Coincident(g64,g70)
    c: Coincident(g63,g67)
FEATURE [PartDesign::Pocket] Pocket014
  BaseFeature = -> Pocket012
  Direction = (0,0,1)
  Length = 2.5
  Length2 = 5
  Profile = -> Sketch043
  ReferenceAxis = -> Sketch043 [N_Axis]
  Refine = true
  Suppressed = false
  Type = 0
FEATURE [PartDesign::Body] Body006  label="CaseC"
  AllowCompound = false
  Group = -> [Sketch021,Pad009,Sketch022,Pocket008,Sketch023,Pocket009,Sketch024,Pocket010,Sketch025,Pocket011,Sketch026,Sketch027,Pad010,Sketch028,Pad011,Sketch029,Pad012,Sketch030,Pad013,Sketch031,Pad014,Sketch032,Pad015,Sketch033,Pad016,Sketch034,Pad017,Chamfer002,DatumPlane001,Sketch035,Pocket012,DatumPlane004,Sketch043,Pocket014]
  Origin = -> Origin006
  Placement = pos=(0,0,11) rot=(0,0,1;0rad)
  Tip = -> Pocket014
FEATURE [Sketcher::SketchObject] Sketch044
  ArcFitTolerance = 1e-06
  AttachmentSupport = -> [DatumPlane003]
  FullyConstrained = true
  MakeInternals = false
  MapMode = 5
  Placement = pos=(9.69e-14,-2.24e-14,0) rot=(-0.490233,0.616308,0.616308;4.0532rad)
  sketch-geometry (5):
    g0: LineSegment [constr] StartX=-115 StartY=0 StartZ=0 EndX=-115 EndY=2 EndZ=0
    g1: LineSegment StartX=-110 StartY=0 StartZ=0 EndX=-90.0004 EndY=0 EndZ=0
    g2: LineSegment StartX=-90.0004 StartY=0 StartZ=0 EndX=-90.0004 EndY=2 EndZ=0
    g3: LineSegment StartX=-90.0004 StartY=2 StartZ=0 EndX=-110 EndY=2 EndZ=0
    g4: LineSegment StartX=-110 StartY=2 StartZ=0 EndX=-110 EndY=0 EndZ=0
  constraints (15):
    c: Distance(g0) = 2
    c: PointOnObject(g0,g-1)
    c: Block(g0)
    c: Coincident(g1,g2)
    c: Coincident(g2,g3)
    c: Coincident(g3,g4)
    c: Coincident(g4,g1)
    c: Horizontal(g1)
    c: Horizontal(g3)
    c: Vertical(g2)
    c: Vertical(g4)
    c: Distance(g2,g4) = 20
    c: Distance(g1,g3) = 2
    c: PointOnObject(g1,g-1)
    c: Distance(g4,g0) = 5
FEATURE [PartDesign::Pad] Pad019
  BaseFeature = -> Pad018
  Direction = (-0.97437,0.224951,0)
  Length = 2
  Length2 = 10
  Profile = -> Sketch044
  ReferenceAxis = -> Sketch044 [N_Axis]
  Refine = true
  Suppressed = false
  Type = 0
FEATURE [PartDesign::Fillet] Fillet
  Base = -> Pad019 [Edge23]
  BaseFeature = -> Pad019
  Radius = 8
  Refine = true
  SupportTransform = false
  Suppressed = false
  UseAllEdges = false
FEATURE [Sketcher::SketchObject] Sketch045
  ArcFitTolerance = 1e-06
  AttachmentSupport = -> [XY_Plane007]
  FullyConstrained = false
  MakeInternals = false
  MapMode = 5
  sketch-geometry (5):
    g0: LineSegment [constr] StartX=0 StartY=0 StartZ=0 EndX=37.5987 EndY=90.7712 EndZ=0
    g1: ArcOfCircle CenterX=0 CenterY=0 CenterZ=0 NormalX=0 NormalY=0 NormalZ=1 AngleXU=0 Radius=83.5 StartAngle=1.01229 EndAngle=1.3439
    g2: ArcOfCircle CenterX=0 CenterY=0 CenterZ=0 NormalX=0 NormalY=0 NormalZ=1 AngleXU=0 Radius=115 StartAngle=1.01229 EndAngle=1.3439
    g3: LineSegment StartX=44.2483 StartY=70.812 StartZ=0 EndX=60.9407 EndY=97.5255 EndZ=0
    g4: LineSegment StartX=18.7834 StartY=81.3599 StartZ=0 EndX=25.8694 EndY=112.053 EndZ=0
  constraints (13):
    c: Distance(g0) = 98.25
    c: Angle(g-1,g0) = 1.1781
    c: Coincident(g0,g-1)
    c: Diameter(g1) = 167
    c: Coincident(g1,g0)
    c: Diameter(g2) = 230
    c: Coincident(g2,g0)
    c: Angle(g3,g0) = 0.165806
    c: Angle(g0,g4) = 0.165806
    c: Coincident(g4,g2)
    c: Coincident(g3,g2)
    c: Coincident(g3,g1)
    c: Coincident(g4,g1)
FEATURE [PartDesign::Pad] Pad020
  Direction = (0,0,1)
  Length = 12
  Length2 = 10
  Profile = -> Sketch045
  ReferenceAxis = -> Sketch045 [N_Axis]
  Refine = true
  Suppressed = false
  Type = 0
FEATURE [PartDesign::Chamfer] Chamfer003
  Angle = 50
  Base = -> Pad020 [Edge7]
  BaseFeature = -> Pad020
  ChamferType = 2
  FlipDirection = false
  Refine = true
  Size = 8
  Size2 = 1
  SupportTransform = false
  Suppressed = false
  UseAllEdges = false
FEATURE [PartDesign::Thickness] Thickness001
  Base = -> Chamfer003 [Face4]
  BaseFeature = -> Chamfer003
  Intersection = false
  Join = 0
  Mode = 0
  Refine = true
  Reversed = true
  SupportTransform = false
  Suppressed = false
  Value = 1
FEATURE [Sketcher::SketchObject] Sketch046
  ArcFitTolerance = 1e-06
  AttachmentSupport = -> [Thickness001]
  FullyConstrained = false
  MakeInternals = false
  MapMode = 5
  Placement = pos=(0,0,11) rot=(1,0,0;3.14159rad)
  sketch-geometry (17):
    g0: LineSegment [constr] StartX=0 StartY=0 StartZ=0 EndX=37.79 EndY=-91.2331 EndZ=0
    g1: Circle CenterX=37.79 CenterY=-91.2331 CenterZ=0 NormalX=0 NormalY=0 NormalZ=1 AngleXU=0 Radius=2.6
    g2: LineSegment StartX=39.5123 StartY=-89.8901 StartZ=0 EndX=38.1215 EndY=-90.452 EndZ=0
    g3: LineSegment StartX=37.5596 StartY=-89.0613 StartZ=0 EndX=36.447 EndY=-89.5108 EndZ=0
    g4: GeomPoint [constr] X=37.79 Y=-91.2331 Z=0
    g5: GeomPoint [constr] X=37.79 Y=-91.2331 Z=0
    g6: LineSegment StartX=36.0677 StartY=-92.5761 StartZ=0 EndX=37.4584 EndY=-92.0142 EndZ=0
    g7: LineSegment StartX=39.9618 StartY=-91.0027 StartZ=0 EndX=39.5123 EndY=-89.8901 EndZ=0
    g8: LineSegment StartX=35.6181 StartY=-91.4635 StartZ=0 EndX=36.0677 EndY=-92.5761 EndZ=0
    g9: GeomPoint [constr] X=37.79 Y=-91.2331 Z=0
    g10: LineSegment StartX=38.0204 StartY=-93.405 StartZ=0 EndX=39.133 EndY=-92.9554 EndZ=0
    g11: LineSegment StartX=39.133 StartY=-92.9554 StartZ=0 EndX=38.5711 EndY=-91.5647 EndZ=0
    g12: LineSegment StartX=36.447 StartY=-89.5108 StartZ=0 EndX=37.0089 EndY=-90.9016 EndZ=0
    g13: LineSegment StartX=37.0089 StartY=-90.9016 StartZ=0 EndX=35.6181 EndY=-91.4635 EndZ=0
    g14: LineSegment StartX=37.4584 StartY=-92.0142 StartZ=0 EndX=38.0204 EndY=-93.405 EndZ=0
    g15: LineSegment StartX=38.1215 StartY=-90.452 StartZ=0 EndX=37.5596 EndY=-89.0613 EndZ=0
    g16: LineSegment StartX=38.5711 StartY=-91.5647 StartZ=0 EndX=39.9618 EndY=-91.0027 EndZ=0
  constraints (25):
    c: Distance(g0) = 98.75
    c: Angle(g-1,g0) = -1.1781
    c: Coincident(g0,g-1)
    c: Diameter(g1) = 5.2
    c: Coincident(g16,g7)
    c: Coincident(g7,g2)
    c: Coincident(g13,g8)
    c: Coincident(g8,g6)
    c: Symmetric(g2,g6,g9)
    c: Distance(g7,g8) = 4.2
    c: Distance(g6,g13) = 1.2
    c: Coincident(g9,g1)
    c: Coincident(g10,g11)
    c: Coincident(g15,g3)
    c: Coincident(g3,g12)
    c: Coincident(g14,g10)
    c: Symmetric(g3,g10,g4)
    c: Distance(g11,g14) = 1.2
    c: Distance(g10,g3) = 4.2
    c: PointOnObject(g2,g15)
    c: Coincident(g12,g13)
    c: PointOnObject(g11,g16)
    c: PointOnObject(g15,g2)
    c: Coincident(g6,g14)
    c: PointOnObject(g16,g11)
FEATURE [PartDesign::Pad] Pad021
  BaseFeature = -> Thickness001
  Direction = (0,0,-1)
  Length = 10
  Length2 = 10
  Profile = -> Sketch046
  ReferenceAxis = -> Sketch046 [N_Axis]
  Refine = true
  Suppressed = false
  Type = 0
FEATURE [PartDesign::Line] DatumLine003
  AttacherType = Attacher::AttachEngineLine
  AttachmentSupport = -> [Pad021]
  Length = 20
  MapMode = 29
  Placement = pos=(7.1e-15,-1.42e-14,0) rot=(0.198716,0.693005,0.693005;2.74927rad)
  ResizeMode = 0
FEATURE [PartDesign::Line] DatumLine004
  AttacherType = Attacher::AttachEngineLine
  AttachmentSupport = -> [Pad021]
  Length = 20
  MapMode = 29
  Placement = pos=(60.9407,97.5255,0) rot=(0,0,1;0rad)
  ResizeMode = 0
FEATURE [PartDesign::Line] DatumLine005
  AttacherType = Attacher::AttachEngineLine
  AttachmentSupport = -> [Pad021]
  Length = 20
  MapMode = 29
  Placement = pos=(44.2483,70.812,0) rot=(0,0,1;0rad)
  ResizeMode = 0
FEATURE [PartDesign::Plane] DatumPlane005
  AttachmentSupport = -> [Pad021]
  Length = 158.666
  MapMode = 5
  Placement = pos=(1.21e-14,-7.5e-15,0) rot=(0.787007,0.436245,0.436245;1.80806rad)
  ResizeMode = 0
  Width = 66.8419
FEATURE [Sketcher::SketchObject] Sketch047
  ArcFitTolerance = 1e-06
  AttachmentSupport = -> [DatumPlane005]
  FullyConstrained = true
  MakeInternals = false
  MapMode = 5
  Placement = pos=(1.21e-14,-7.5e-15,0) rot=(0.787007,0.436245,0.436245;1.80806rad)
FEATURE [Sketcher::SketchObject] Sketch048
  ArcFitTolerance = 1e-06
  AttachmentSupport = -> [DatumPlane005]
  FullyConstrained = true
  MakeInternals = false
  MapMode = 5
  Placement = pos=(1.21e-14,-7.5e-15,0) rot=(0.787007,0.436245,0.436245;1.80806rad)
  sketch-geometry (5):
    g0: LineSegment StartX=99.0001 StartY=0 StartZ=0 EndX=99.0001 EndY=2 EndZ=0
    g1: LineSegment StartX=99.0001 StartY=2 StartZ=0 EndX=94.0001 EndY=2 EndZ=0
    g2: LineSegment StartX=94.0001 StartY=2 StartZ=0 EndX=94.0001 EndY=0 EndZ=0
    g3: LineSegment StartX=94.0001 StartY=0 StartZ=0 EndX=99.0001 EndY=0 EndZ=0
    g4: LineSegment [constr] StartX=115 StartY=0 StartZ=0 EndX=115 EndY=2 EndZ=0
  constraints (15):
    c: Coincident(g0,g1)
    c: Coincident(g1,g2)
    c: Coincident(g2,g3)
    c: Coincident(g3,g0)
    c: Vertical(g0)
    c: Vertical(g2)
    c: Horizontal(g1)
    c: Horizontal(g3)
    c: PointOnObject(g0,g-1)
    c: Distance(g0,g2) = 5
    c: Distance(g4) = 2
    c: PointOnObject(g4,g-1)
    c: Block(g4)
    c: Distance(g0,g4) = 16
    c: Distance(g2,g2) = 2
FEATURE [PartDesign::Pad] Pad022
  BaseFeature = -> Pad021
  Direction = (0.848048,-0.529919,-1e-16)
  Length = 2
  Length2 = 10
  Profile = -> Sketch048
  ReferenceAxis = -> Sketch048 [N_Axis]
  Refine = true
  Suppressed = false
  Type = 0
FEATURE [PartDesign::Plane] DatumPlane006
  AttachmentSupport = -> [Pad022]
  Length = 149.534
  MapMode = 5
  Placement = pos=(-6.9e-15,1.6e-15,0) rot=(-0.490233,0.616308,0.616308;4.0532rad)
  ResizeMode = 0
  Width = 66.3225
FEATURE [Sketcher::SketchObject] Sketch049
  ArcFitTolerance = 1e-06
  AttachmentSupport = -> [DatumPlane006]
  FullyConstrained = true
  MakeInternals = false
  MapMode = 5
  Placement = pos=(-6.9e-15,1.6e-15,0) rot=(-0.490233,0.616308,0.616308;4.0532rad)
  sketch-geometry (5):
    g0: LineSegment [constr] StartX=-115 StartY=0 StartZ=0 EndX=-115 EndY=2 EndZ=0
    g1: LineSegment StartX=-110 StartY=0 StartZ=0 EndX=-90.0004 EndY=0 EndZ=0
    g2: LineSegment StartX=-90.0004 StartY=0 StartZ=0 EndX=-90.0004 EndY=2 EndZ=0
    g3: LineSegment StartX=-90.0004 StartY=2 StartZ=0 EndX=-110 EndY=2 EndZ=0
    g4: LineSegment StartX=-110 StartY=2 StartZ=0 EndX=-110 EndY=0 EndZ=0
  constraints (15):
    c: Distance(g0) = 2
    c: PointOnObject(g0,g-1)
    c: Block(g0)
    c: Coincident(g1,g2)
    c: Coincident(g2,g3)
    c: Coincident(g3,g4)
    c: Coincident(g4,g1)
    c: Horizontal(g1)
    c: Horizontal(g3)
    c: Vertical(g2)
    c: Vertical(g4)
    c: Distance(g2,g4) = 20
    c: Distance(g1,g3) = 2
    c: PointOnObject(g1,g-1)
    c: Distance(g4,g0) = 5
FEATURE [PartDesign::Pad] Pad023
  BaseFeature = -> Pad022
  Direction = (-0.97437,0.224951,1e-16)
  Length = 2
  Length2 = 10
  Profile = -> Sketch049
  ReferenceAxis = -> Sketch049 [N_Axis]
  Refine = true
  Suppressed = false
  Type = 0
FEATURE [PartDesign::Fillet] Fillet003
  Base = -> Pad023 [Edge23]
  BaseFeature = -> Pad023
  Radius = 8
  Refine = true
  SupportTransform = false
  Suppressed = false
  UseAllEdges = false
FEATURE [PartDesign::Fillet] Fillet004
  Base = -> Fillet003 [Edge1,Edge2,Edge4,Edge13,Edge15,Edge19]
  BaseFeature = -> Fillet003
  Radius = 5
  Refine = true
  SupportTransform = false
  Suppressed = false
  UseAllEdges = false
FEATURE [Sketcher::SketchObject] Sketch050
  ArcFitTolerance = 1e-06
  FullyConstrained = false
  MakeInternals = false
  MapMode = 5
  Placement = pos=(1.21e-14,-7.5e-15,0) rot=(0.787007,0.436245,0.436245;1.80806rad)
  sketch-geometry (4):
    g0: LineSegment StartX=114.029 StartY=0 StartZ=0 EndX=114.029 EndY=5 EndZ=0
    g1: LineSegment StartX=114.029 StartY=5 StartZ=0 EndX=99.0294 EndY=5 EndZ=0
    g2: LineSegment StartX=99.0294 StartY=5 StartZ=0 EndX=99.0294 EndY=0 EndZ=0
    g3: LineSegment StartX=99.0294 StartY=0 StartZ=0 EndX=114.029 EndY=0 EndZ=0
  constraints (11):
    c: Coincident(g0,g1)
    c: Coincident(g1,g2)
    c: Coincident(g2,g3)
    c: Coincident(g3,g0)
    c: Vertical(g0)
    c: Vertical(g2)
    c: Horizontal(g1)
    c: Horizontal(g3)
    c: Distance(g0,g2) = 15
    c: Distance(g1,g3) = 5
    c: PointOnObject(g0,g-1)
FEATURE [Sketcher::SketchObject] Sketch052
  ArcFitTolerance = 1e-06
  FullyConstrained = false
  MakeInternals = false
  MapMode = 5
  Placement = pos=(44.211,106.735,5.49372) rot=(0.639476,0.427284,0.639138;3.94882rad)
  sketch-geometry (4):
    g0: ArcOfCircle CenterX=-5.53491 CenterY=-10 CenterZ=0 NormalX=0 NormalY=0 NormalZ=1 AngleXU=0 Radius=5 StartAngle=3.14159 EndAngle=6.28319
    g1: ArcOfCircle CenterX=-5.53491 CenterY=10 CenterZ=0 NormalX=0 NormalY=0 NormalZ=1 AngleXU=0 Radius=5 StartAngle=0 EndAngle=3.14159
    g2: LineSegment StartX=-10.5349 StartY=-10 StartZ=0 EndX=-10.5349 EndY=10 EndZ=0
    g3: LineSegment StartX=-0.534909 StartY=-10 StartZ=0 EndX=-0.534909 EndY=10 EndZ=0
  constraints (9):
    c: Tangent(g0,g2) = 1.5708
    c: Tangent(g0,g3) = -1.5708
    c: Tangent(g1,g2) = 1.5708
    c: Tangent(g1,g3) = -1.5708
    c: Equal(g0,g1)
    c: Vertical(g3)
    c: Distance(g0,g1) = 20
    c: Radius(g0) = 5
    c: Distance(g0,g-1) = 10
FEATURE [PartDesign::Fillet] Fillet006
  Base = -> Fillet [Edge19,Edge15,Edge13,Edge4,Edge2,Edge1]
  BaseFeature = -> Fillet
  Radius = 4
  Refine = true
  SupportTransform = false
  Suppressed = false
  UseAllEdges = false
FEATURE [PartDesign::Fillet] Fillet007
  Base = -> Fillet006 [Edge60,Edge66,Edge67,Edge61]
  BaseFeature = -> Fillet006
  Radius = 5
  Refine = true
  SupportTransform = false
  Suppressed = false
  UseAllEdges = false
FEATURE [PartDesign::Body] Body005  label="Button"
  AllowCompound = false
  Group = -> [Sketch014,Pad006,Chamfer,Thickness,Sketch015,Pad007,DatumPlane002,DatumLine,DatumLine001,DatumLine002,Sketch040,Sketch041,Pad018,DatumPlane003,Sketch044,Pad019,Fillet,Fillet006,Fillet007]
  Origin = -> Origin005
  Placement = pos=(0,0,100) rot=(0,0,1;0rad)
  Tip = -> Fillet007
FEATURE [PartDesign::Fillet] Fillet008
  Base = -> Fillet004 [Edge67,Edge66,Edge65,Edge61,Edge60,Edge59]
  BaseFeature = -> Fillet004
  Radius = 5
  Refine = true
  SupportTransform = false
  Suppressed = false
  UseAllEdges = false
FEATURE [Sketcher::SketchObject] Sketch051
  ArcFitTolerance = 1e-06
  FullyConstrained = true
  MakeInternals = false
  MapMode = 5
  Placement = pos=(1.21e-14,-7.5e-15,0) rot=(0.787007,0.436245,0.436245;1.80806rad)
FEATURE [PartDesign::Pocket] Pocket017
  BaseFeature = -> Fillet008
  Direction = (-0.848048,0.529919,1e-16)
  Length = 5
  Length2 = 5
  Profile = -> Sketch050
  ReferenceAxis = -> Sketch050 [N_Axis]
  Refine = true
  Suppressed = false
  Type = 0
FEATURE [PartDesign::Pocket] Pocket016
  BaseFeature = -> Pocket017
  Direction = (-0.382684,-0.923879,0.000528895)
  Length = 5
  Length2 = 5
  Profile = -> Sketch052
  ReferenceAxis = -> Sketch052 [N_Axis]
  Refine = true
  Suppressed = false
  Type = 0
FEATURE [PartDesign::Body] Body007  label="ButtonHoled"
  AllowCompound = false
  Group = -> [Sketch045,Pad020,Chamfer003,Thickness001,Sketch046,Pad021,DatumPlane005,DatumLine003,DatumLine004,DatumLine005,Sketch047,Sketch048,Pad022,DatumPlane006,Sketch049,Pad023,Fillet003,Fillet004,Sketch052,Fillet008,Sketch051,Pocket017,Pocket016,Sketch050]
  Origin = -> Origin007
  Placement = pos=(0,0,100) rot=(0,0,1;0rad)
  Tip = -> Pocket017
